FREECAD ASSEMBLY — COMPONENT RECIPES ("feeder_assembly")

This assembly document has 52 components, labeled P0..P51 below (a component is one placed body or linked part). 40 of them carry a construction recipe — the FreeCAD feature program that regenerates the part from scratch, quoted from this document or its linked companion documents; the rest are supplied as boundary geometry only. No exploded tour is included for this assembly.
NOTE — this tour is split across 3 documents so each fits a 32k-token context. This is document 1: the component sections continue in the remaining 2 documents, each repeating the header above.
COMPONENT P0 — recipe-attached ("Slide-left-Body", modeled in this document).
Construction recipe (the document's own serialized feature program — sketch geometry with constraints, then the solid features built on it; lengths are millimeters unless a unit is written):

FEATURE [Sketcher::SketchObject] Sketch
  FullyConstrained = true
  MapMode = 5
  Placement = pos=(0,0,0) rot=(0.57735,0.57735,0.57735;2.0944rad)
  Support = -> [YZ_Plane]
  sketch-geometry (4):
    g0: LineSegment StartX=0 StartY=0 StartZ=0 EndX=20 EndY=0 EndZ=0
    g1: LineSegment StartX=20 StartY=0 StartZ=0 EndX=20 EndY=30 EndZ=0
    g2: LineSegment StartX=20 StartY=30 StartZ=0 EndX=0 EndY=30 EndZ=0
    g3: LineSegment StartX=0 StartY=30 StartZ=0 EndX=0 EndY=0 EndZ=0
  constraints (11):
    c: Coincident(g0,g1)
    c: Coincident(g1,g2)
    c: Coincident(g2,g3)
    c: Coincident(g3,g0)
    c: Horizontal(g0)
    c: Horizontal(g2)
    c: Vertical(g1)
    c: Vertical(g3)
    c: Coincident(g0,g-1)
    c: DistanceY(g3,g3) = 30
    c: DistanceX(g0,g0) = 20
FEATURE [PartDesign::Pad] Pad  label="Pad-body001"
  Direction = (1,-2e-16,3e-16)
  Length = 200
  Length2 = 10
  Placement = pos=(0,0,0) rot=(0.57735,0.57735,0.57735;2.0944rad)
  Profile = -> Sketch
  ReferenceAxis = -> Sketch [N_Axis]
  Type = 0
FEATURE [Sketcher::SketchObject] Sketch008
  FullyConstrained = true
  MapMode = 5
  Placement = pos=(8.8e-15,20,-4.4e-15) rot=(0.57735,0.57735,0.57735;4.18879rad)
  Support = -> [Pad]
  sketch-geometry (5):
    g0: Circle CenterX=15 CenterY=10 CenterZ=0 NormalX=0 NormalY=0 NormalZ=1 AngleXU=0 Radius=5
    g1: ArcOfCircle CenterX=15 CenterY=190 CenterZ=0 NormalX=0 NormalY=0 NormalZ=1 AngleXU=0 Radius=5 StartAngle=1.7e-15 EndAngle=3.14159
    g2: ArcOfCircle CenterX=15 CenterY=35 CenterZ=0 NormalX=0 NormalY=0 NormalZ=1 AngleXU=0 Radius=5 StartAngle=3.14159 EndAngle=6.28319
    g3: LineSegment StartX=10 StartY=190 StartZ=0 EndX=10 EndY=35 EndZ=0
    g4: LineSegment StartX=20 StartY=35 StartZ=0 EndX=20 EndY=190 EndZ=0
  constraints (13):
    c: Diameter(g0) = 10
    c: DistanceX(g-1,g0) = 15
    c: DistanceY(g-1,g0) = 10
    c: Tangent(g1,g3) = -1.5708
    c: Tangent(g3,g2) = -1.5708
    c: Tangent(g2,g4) = -1.5708
    c: Tangent(g4,g1) = -1.5708
    c: Equal(g1,g2)
    c: Vertical(g3)
    c: Radius(g2) = 5
    c: Vertical(g2,g0)
    c: DistanceY(g0,g2) = 25
    c: DistanceY(g0,g1) = 180
FEATURE [PartDesign::Pocket] Pocket  label="Pocket-slider_guide"
  BaseFeature = -> Pad
  Direction = (-3e-16,-1,1e-16)
  Length = 5
  Length2 = 5
  Placement = pos=(0,0,0) rot=(0.57735,0.57735,0.57735;2.0944rad)
  Profile = -> Sketch008
  ReferenceAxis = -> Sketch008 [N_Axis]
  Type = 1
FEATURE [Sketcher::SketchObject] Sketch009
  FullyConstrained = true
  MapMode = 5
  Placement = pos=(-8.4e-15,1.32e-14,30) rot=(0,0,-1;1.5708rad)
  Support = -> [Pocket]
  sketch-geometry (2):
    g0: Circle CenterX=-10 CenterY=50 CenterZ=0 NormalX=0 NormalY=0 NormalZ=1 AngleXU=0 Radius=3.1
    g1: Circle CenterX=-10 CenterY=180 CenterZ=0 NormalX=0 NormalY=0 NormalZ=1 AngleXU=0 Radius=3.1
  constraints (6):
    c: DistanceX(g0,g-1) = 10
    c: Vertical(g1,g0)
    c: DistanceY(g-1,g0) = 50
    c: DistanceY(g0,g1) = 130
    c: Diameter(g0) = 6.2
    c: Equal(g1,g0)
FEATURE [PartDesign::Pocket] Pocket001  label="Pocket-mount_holes"
  BaseFeature = -> Pocket
  Direction = (3e-16,-5e-16,-1)
  Length = 26.5
  Length2 = 5
  Placement = pos=(0,0,0) rot=(0.57735,0.57735,0.57735;2.0944rad)
  Profile = -> Sketch009
  ReferenceAxis = -> Sketch009 [N_Axis]
  Type = 0
FEATURE [Sketcher::SketchObject] Sketch013  label="Sketch-slider_guide_line"
  FullyConstrained = false
  MapMode = 5
  Placement = pos=(0,1e-16,0) rot=(-0.57735,-0.57735,0.57735;4.18879rad)
  Support = -> [Pocket001]
  sketch-geometry (1):
    g0: LineSegment StartX=-14.7121 StartY=24.4994 StartZ=0 EndX=-14.7121 EndY=187.74 EndZ=0
  constraints (1):
    c: Vertical(g0)
FEATURE [Sketcher::SketchObject] Sketch023
  ExternalGeometry = -> [Pocket001]
  FullyConstrained = true
  MapMode = 5
  Placement = pos=(0,0,0) rot=(0.57735,0.57735,-0.57735;4.18879rad)
  Support = -> [Pocket001]
  sketch-geometry (8):
    g0: LineSegment StartX=-10 StartY=2.5 StartZ=0 EndX=-10 EndY=-52.5 EndZ=0
    g1: LineSegment StartX=0 StartY=0 StartZ=0 EndX=0 EndY=-30 EndZ=0
    g2: LineSegment StartX=0 StartY=-30 StartZ=0 EndX=20 EndY=-30 EndZ=0
    g3: GeomPoint X=0 Y=-15 Z=0
    g4: LineSegment StartX=4.24533 StartY=-52.5 StartZ=0 EndX=20 EndY=-30 EndZ=0
    g5: LineSegment StartX=-10 StartY=-52.5 StartZ=0 EndX=4.24533 EndY=-52.5 EndZ=0
    g6: LineSegment StartX=0 StartY=0 StartZ=0 EndX=-5 EndY=2.5 EndZ=0
    g7: LineSegment StartX=-5 StartY=2.5 StartZ=0 EndX=-10 EndY=2.5 EndZ=0
  constraints (20):
    c: Coincident(g6,g-4)
    c: Vertical(g0)
    c: Coincident(g5,g0)
    c: Coincident(g1,g6)
    c: Coincident(g0,g7)
    c: Coincident(g1,g2)
    c: Coincident(g1,g-4)
    c: DistanceX(g7,g6) = 10
    c: DistanceY(g0,g0) = 55
    c: PointOnObject(g3,g1)
    c: DistanceY(g3,g6) = 15
    c: DistanceY(g3,g7) = 17.5
    c: Horizontal(g5)
    c: Coincident(g5,g4)
    c: Coincident(g2,g4)
    c: Coincident(g2,g-3)
    c: Angle(g2,g4) = 0.959931
    c: Coincident(g6,g7)
    c: Horizontal(g7)
    c: DistanceX(g0,g6) = 5
FEATURE [PartDesign::Pad] Pad011
  BaseFeature = -> Pocket001
  Direction = (-1,2e-16,-2e-16)
  Length = 20
  Length2 = 10
  Placement = pos=(0,0,0) rot=(0.57735,0.57735,0.57735;2.0944rad)
  Profile = -> Sketch023
  ReferenceAxis = -> Sketch023 [N_Axis]
  Reversed = true
  Type = 0
FEATURE [Sketcher::SketchObject] Sketch025
  ExternalGeometry = -> [Pad011]
  FullyConstrained = true
  MapMode = 5
  Placement = pos=(-2.2e-15,-10,6e-16) rot=(-0.57735,-0.57735,0.57735;4.18879rad)
  Support = -> [Pad011]
  sketch-geometry (15):
    g0: Circle CenterX=-49.575 CenterY=14.9 CenterZ=0 NormalX=0 NormalY=0 NormalZ=1 AngleXU=0 Radius=1.125
    g1: Circle CenterX=-49.575 CenterY=5.1 CenterZ=0 NormalX=0 NormalY=0 NormalZ=1 AngleXU=0 Radius=1.125
    g2: Circle CenterX=-1.125 CenterY=14.9 CenterZ=0 NormalX=0 NormalY=0 NormalZ=1 AngleXU=0 Radius=1.125
    g3: Circle CenterX=-1.125 CenterY=5.1 CenterZ=0 NormalX=0 NormalY=0 NormalZ=1 AngleXU=0 Radius=1.125
    g4: LineSegment StartX=-46.35 StartY=0 StartZ=0 EndX=-4.35 EndY=0 EndZ=0
    g5: LineSegment StartX=-4.35 StartY=0 StartZ=0 EndX=-4.35 EndY=20 EndZ=0
    g6: LineSegment StartX=-4.35 StartY=20 StartZ=0 EndX=-46.35 EndY=20 EndZ=0
    g7: LineSegment StartX=-46.35 StartY=20 StartZ=0 EndX=-46.35 EndY=0 EndZ=0
    g8: LineSegment StartX=-49.575 StartY=14.9 StartZ=0 EndX=-49.575 EndY=5.1 EndZ=0
    g9: LineSegment StartX=-49.575 StartY=5.1 StartZ=0 EndX=-1.125 EndY=5.1 EndZ=0
    g10: LineSegment StartX=-1.125 StartY=14.9 StartZ=0 EndX=-49.575 EndY=14.9 EndZ=0
    g11: LineSegment StartX=-46.35 StartY=20 StartZ=0 EndX=-49.575 EndY=14.9 EndZ=0
    g12: LineSegment StartX=-4.35 StartY=20 StartZ=0 EndX=-1.125 EndY=14.9 EndZ=0
    g13: LineSegment StartX=-1.125 StartY=5.1 StartZ=0 EndX=-1.125 EndY=10 EndZ=0
    g14: LineSegment StartX=-1.125 StartY=10 StartZ=0 EndX=-1.125 EndY=14.9 EndZ=0
  constraints (39):
    c: Tangent(g3,g-2)
    c: Coincident(g4,g5)
    c: Coincident(g5,g6)
    c: Coincident(g6,g7)
    c: Coincident(g7,g4)
    c: Horizontal(g4)
    c: Horizontal(g6)
    c: Vertical(g5)
    c: Vertical(g7)
    c: Horizontal(g-4,g5)
    c: DistanceX(g6,g6) = 42
    c: Diameter(g2) = 2.25
    c: Equal(g0,g1)
    c: Equal(g1,g3)
    c: Equal(g3,g2)
    c: Coincident(g8,g0)
    c: Coincident(g8,g1)
    c: Vertical(g8)
    c: Coincident(g9,g1)
    c: Coincident(g9,g3)
    c: Horizontal(g9)
    c: Coincident(g13,g3)
    c: Coincident(g14,g2)
    c: Coincident(g10,g2)
    c: Coincident(g10,g0)
    c: Horizontal(g10)
    c: Coincident(g11,g6)
    c: Coincident(g11,g0)
    c: Coincident(g12,g5)
    c: Coincident(g12,g2)
    c: Equal(g12,g11)
    c: DistanceX(g9,g9) = 48.45
    c: DistanceY(g8,g8) = 9.8
    c: Coincident(g13,g14)
    c: Vertical(g13)
    c: Vertical(g14)
    c: Equal(g14,g13)
    c: DistanceY(g-4,g13) = 10
    c: PointOnObject(g4,g-5)
FEATURE [PartDesign::Pocket] Pocket008
  BaseFeature = -> Pad011
  Direction = (1e-16,1,1e-16)
  Length = 10
  Length2 = 5
  Placement = pos=(0,0,0) rot=(0.57735,0.57735,0.57735;2.0944rad)
  Profile = -> Sketch025
  ReferenceAxis = -> Sketch025 [N_Axis]
  Type = 0
FEATURE [Sketcher::SketchObject] Sketch026
  ExternalGeometry = -> [Pocket008]
  FullyConstrained = true
  MapMode = 5
  Placement = pos=(-1.47e-14,0,52.5) rot=(0,0,-1;1.5708rad)
  Support = -> [Pocket008]
  sketch-geometry (4):
    g0: LineSegment StartX=-20 StartY=17.5 StartZ=0 EndX=5 EndY=17.5 EndZ=0
    g1: LineSegment StartX=5 StartY=17.5 StartZ=0 EndX=5 EndY=2.5 EndZ=0
    g2: LineSegment StartX=5 StartY=2.5 StartZ=0 EndX=-20 EndY=2.5 EndZ=0
    g3: LineSegment StartX=-20 StartY=2.5 StartZ=0 EndX=-20 EndY=17.5 EndZ=0
  constraints (12):
    c: Coincident(g0,g1)
    c: Coincident(g1,g2)
    c: Coincident(g2,g3)
    c: Coincident(g3,g0)
    c: Horizontal(g0)
    c: Horizontal(g2)
    c: Vertical(g1)
    c: Vertical(g3)
    c: DistanceX(g2,g2) = 25
    c: DistanceX(g1,g-3) = 5
    c: DistanceY(g-3,g1) = 2.5
    c: DistanceY(g0,g-4) = 2.5
FEATURE [PartDesign::Pocket] Pocket009
  BaseFeature = -> Pocket008
  Direction = (3e-16,-1e-16,-1)
  Length = 6
  Length2 = 5
  Placement = pos=(0,0,0) rot=(0.57735,0.57735,0.57735;2.0944rad)
  Profile = -> Sketch026
  ReferenceAxis = -> Sketch026 [N_Axis]
  Type = 0
FEATURE [Sketcher::SketchObject] Sketch027
  ExternalGeometry = -> [Pocket009]
  FullyConstrained = true
  MapMode = 5
  Placement = pos=(7e-16,0,-2.5) rot=(0.707107,0.707107,0;3.14159rad)
  Support = -> [Pocket009]
  sketch-geometry (4):
    g0: LineSegment StartX=-5 StartY=17.5 StartZ=0 EndX=5 EndY=17.5 EndZ=0
    g1: LineSegment StartX=5 StartY=17.5 StartZ=0 EndX=5 EndY=2.5 EndZ=0
    g2: LineSegment StartX=5 StartY=2.5 StartZ=0 EndX=-5 EndY=2.5 EndZ=0
    g3: LineSegment StartX=-5 StartY=2.5 StartZ=0 EndX=-5 EndY=17.5 EndZ=0
  constraints (12):
    c: Coincident(g0,g1)
    c: Coincident(g1,g2)
    c: Coincident(g2,g3)
    c: Coincident(g3,g0)
    c: Horizontal(g0)
    c: Horizontal(g2)
    c: Vertical(g1)
    c: Vertical(g3)
    c: DistanceX(g-3,g2) = 5
    c: DistanceY(g-3,g2) = 2.5
    c: DistanceY(g0,g-3) = 2.5
    c: DistanceX(g0,g0) = 10
FEATURE [PartDesign::Pocket] Pocket010
  BaseFeature = -> Pocket009
  Direction = (-3e-16,1e-16,1)
  Length = 6
  Length2 = 5
  Placement = pos=(0,0,0) rot=(0.57735,0.57735,0.57735;2.0944rad)
  Profile = -> Sketch027
  ReferenceAxis = -> Sketch027 [N_Axis]
  Type = 0
FEATURE [Sketcher::SketchObject] Sketch030
  FullyConstrained = true
  MapMode = 5
  Placement = pos=(-8.4e-15,1.32e-14,30) rot=(0,0,-1;1.5708rad)
  Support = -> [Pocket010]
  sketch-geometry (8):
    g0: ArcOfCircle CenterX=-10 CenterY=40 CenterZ=0 NormalX=0 NormalY=0 NormalZ=1 AngleXU=0 Radius=6 StartAngle=3.14159 EndAngle=6.28319
    g1: ArcOfCircle CenterX=-10 CenterY=80 CenterZ=0 NormalX=0 NormalY=0 NormalZ=1 AngleXU=0 Radius=6 StartAngle=-1.8e-15 EndAngle=3.14159
    g2: LineSegment StartX=-4 StartY=40 StartZ=0 EndX=-4 EndY=80 EndZ=0
    g3: LineSegment StartX=-16 StartY=80 StartZ=0 EndX=-16 EndY=40 EndZ=0
    g4: ArcOfCircle CenterX=-10 CenterY=180 CenterZ=0 NormalX=0 NormalY=0 NormalZ=1 AngleXU=0 Radius=6 StartAngle=2.9e-15 EndAngle=3.14159
    g5: ArcOfCircle CenterX=-10 CenterY=140 CenterZ=0 NormalX=0 NormalY=0 NormalZ=1 AngleXU=0 Radius=6 StartAngle=3.14159 EndAngle=6.28319
    g6: LineSegment StartX=-16 StartY=180 StartZ=0 EndX=-16 EndY=140 EndZ=0
    g7: LineSegment StartX=-4 StartY=140 StartZ=0 EndX=-4 EndY=180 EndZ=0
  constraints (20):
    c: Tangent(g0,g2) = -1.5708
    c: Tangent(g2,g1) = -1.5708
    c: Tangent(g1,g3) = -1.5708
    c: Tangent(g3,g0) = -1.5708
    c: Equal(g0,g1)
    c: Vertical(g2)
    c: Diameter(g1) = 12
    c: DistanceY(g2,g2) = 40
    c: DistanceX(g-1,g0) = -10
    c: DistanceY(g-1,g0) = 40
    c: Tangent(g4,g6) = -1.5708
    c: Tangent(g6,g5) = -1.5708
    c: Tangent(g5,g7) = -1.5708
    c: Tangent(g7,g4) = -1.5708
    c: Equal(g4,g5)
    c: Vertical(g6)
    c: DistanceY(g1,g5) = 60
    c: DistanceY(g7,g7) = 40
    c: Diameter(g5) = 12
    c: Vertical(g5,g1)
FEATURE [PartDesign::Pocket] Pocket012
  BaseFeature = -> Pocket010
  Direction = (3e-16,-8e-16,-1)
  Length = 26.5
  Length2 = 5
  Placement = pos=(0,0,0) rot=(0.57735,0.57735,0.57735;2.0944rad)
  Profile = -> Sketch030
  ReferenceAxis = -> Sketch030 [N_Axis]
  Type = 0
FEATURE [Sketcher::SketchObject] Sketch031
  FullyConstrained = true
  MapMode = 5
  Placement = pos=(-8.4e-15,1.32e-14,30) rot=(0,0,-1;1.5708rad)
  Support = -> [Pocket012]
  sketch-geometry (4):
    g0: Circle CenterX=-10 CenterY=45 CenterZ=0 NormalX=0 NormalY=0 NormalZ=1 AngleXU=0 Radius=3.1
    g1: Circle CenterX=-10 CenterY=75 CenterZ=0 NormalX=0 NormalY=0 NormalZ=1 AngleXU=0 Radius=3.1
    g2: Circle CenterX=-10 CenterY=145 CenterZ=0 NormalX=0 NormalY=0 NormalZ=1 AngleXU=0 Radius=3.1
    g3: Circle CenterX=-10 CenterY=175 CenterZ=0 NormalX=0 NormalY=0 NormalZ=1 AngleXU=0 Radius=3.1
  constraints (12):
    c: Equal(g0,g1)
    c: Equal(g1,g2)
    c: Equal(g2,g3)
    c: Vertical(g3,g2)
    c: Vertical(g2,g1)
    c: Vertical(g1,g0)
    c: DistanceX(g0,g-1) = 10
    c: DistanceY(g-1,g0) = 45
    c: DistanceY(g0,g1) = 30
    c: DistanceY(g1,g2) = 70
    c: DistanceY(g2,g3) = 30
    c: Diameter(g2) = 6.2
FEATURE [PartDesign::Pocket] Pocket013
  BaseFeature = -> Pocket012
  Direction = (3e-16,-8e-16,-1)
  Length = 5
  Length2 = 5
  Placement = pos=(0,0,0) rot=(0.57735,0.57735,0.57735;2.0944rad)
  Profile = -> Sketch031
  ReferenceAxis = -> Sketch031 [N_Axis]
  Type = 1
FEATURE [Sketcher::SketchObject] Sketch032
  ExternalGeometry = -> [Pocket013]
  FullyConstrained = true
  MapMode = 5
  Placement = pos=(-1.47e-14,0,52.5) rot=(0,0,-1;1.5708rad)
  Support = -> [Pocket013]
  sketch-geometry (6):
    g0: LineSegment StartX=10 StartY=11 StartZ=0 EndX=8 EndY=11 EndZ=0
    g1: LineSegment StartX=8 StartY=11 StartZ=0 EndX=8 EndY=9 EndZ=0
    g2: LineSegment StartX=8 StartY=9 StartZ=0 EndX=10 EndY=9 EndZ=0
    g3: LineSegment StartX=10 StartY=9 StartZ=0 EndX=10 EndY=11 EndZ=0
    g4: LineSegment StartX=10 StartY=20 StartZ=0 EndX=8 EndY=11 EndZ=0
    g5: LineSegment StartX=8 StartY=9 StartZ=0 EndX=10 EndY=-3.6e-15 EndZ=0
  constraints (16):
    c: Coincident(g0,g1)
    c: Coincident(g1,g2)
    c: Coincident(g2,g3)
    c: Coincident(g3,g0)
    c: Horizontal(g0)
    c: Horizontal(g2)
    c: Vertical(g1)
    c: Vertical(g3)
    c: PointOnObject(g0,g-3)
    c: DistanceX(g2,g2) = 2
    c: DistanceY(g1,g1) = 2
    c: Coincident(g4,g-3)
    c: Coincident(g4,g0)
    c: Coincident(g5,g1)
    c: Coincident(g5,g-3)
    c: Equal(g4,g5)
FEATURE [PartDesign::Pocket] Pocket014
  BaseFeature = -> Pocket013
  Direction = (3e-16,-3e-16,-1)
  Length = 5
  Length2 = 5
  Placement = pos=(0,0,0) rot=(0.57735,0.57735,0.57735;2.0944rad)
  Profile = -> Sketch032
  ReferenceAxis = -> Sketch032 [N_Axis]
  Type = 1
FEATURE [PartDesign::Body] Body  label="Slide-left-Body"
  Group = -> [Sketch,Pad,Sketch008,Pocket,Sketch009,Pocket001,Sketch013,Sketch023,Pad011,Sketch025,Pocket008,Sketch026,Pocket009,Sketch027,Pocket010,Sketch030,Pocket012,Sketch031,Pocket013,Sketch032,Pocket014]
  Origin = -> Origin
  Placement = pos=(-375,53,160) rot=(0,0,-1;1.5708rad)
  Tip = -> Pocket014
COMPONENT P1 — recipe-attached ("Door-back-Body", modeled in this document).
Construction recipe (the document's own serialized feature program — sketch geometry with constraints, then the solid features built on it; lengths are millimeters unless a unit is written):

FEATURE [Sketcher::SketchObject] Sketch001
  FullyConstrained = true
  MapMode = 5
  Support = -> [XY_Plane001]
  sketch-geometry (4):
    g0: LineSegment StartX=0 StartY=50 StartZ=0 EndX=166 EndY=50 EndZ=0
    g1: LineSegment StartX=166 StartY=50 StartZ=0 EndX=166 EndY=140 EndZ=0
    g2: LineSegment StartX=166 StartY=140 StartZ=0 EndX=0 EndY=140 EndZ=0
    g3: LineSegment StartX=0 StartY=140 StartZ=0 EndX=0 EndY=50 EndZ=0
  constraints (12):
    c: Coincident(g0,g1)
    c: Coincident(g1,g2)
    c: Coincident(g2,g3)
    c: Coincident(g3,g0)
    c: Horizontal(g0)
    c: Horizontal(g2)
    c: Vertical(g1)
    c: Vertical(g3)
    c: PointOnObject(g0,g-2)
    c: DistanceY(g1,g1) = 90
    c: DistanceX(g0,g0) = 166
    c: DistanceY(g-1,g2) = 140
FEATURE [PartDesign::Pad] Pad001  label="Pad-base_rect"
  Direction = (0,0,1)
  Length = 5
  Length2 = 10
  Profile = -> Sketch001
  ReferenceAxis = -> Sketch001 [N_Axis]
  Type = 0
FEATURE [Sketcher::SketchObject] Sketch002
  ExternalGeometry = -> [Pad001]
  FullyConstrained = true
  MapMode = 5
  Placement = pos=(0,0,0) rot=(0.57735,-0.57735,-0.57735;2.0944rad)
  Support = -> [Pad001]
  sketch-geometry (1):
    g0: Circle CenterX=-140 CenterY=2.5 CenterZ=0 NormalX=0 NormalY=0 NormalZ=1 AngleXU=0 Radius=4.5
  constraints (3):
    c: DistanceY(g-3,g0) = 2.5
    c: Diameter(g0) = 9
    c: PointOnObject(g0,g-3)
FEATURE [PartDesign::Pad] Pad002  label="Pad-base_9mm_shaft"
  BaseFeature = -> Pad001
  Direction = (-1,0,0)
  Length = 21
  Length2 = 177
  Profile = -> Sketch002
  ReferenceAxis = -> Sketch002 [N_Axis]
  Type = 4
FEATURE [Sketcher::SketchObject] Sketch014
  ExternalGeometry = -> [Pad002]
  FullyConstrained = true
  MapMode = 5
  Placement = pos=(0,0,0) rot=(1,0,0;3.14159rad)
  Support = -> [Pad002]
  sketch-geometry (18):
    g0: LineSegment StartX=10 StartY=-45.5 StartZ=0 EndX=15 EndY=-45.5 EndZ=0
    g1: LineSegment StartX=15 StartY=-45.5 StartZ=0 EndX=15 EndY=-60.5 EndZ=0
    g2: LineSegment StartX=15 StartY=-60.5 StartZ=0 EndX=10 EndY=-60.5 EndZ=0
    g3: LineSegment StartX=10 StartY=-60.5 StartZ=0 EndX=10 EndY=-45.5 EndZ=0
    g4: LineSegment StartX=25.5 StartY=-45.5 StartZ=0 EndX=30.5 EndY=-45.5 EndZ=0
    g5: LineSegment StartX=30.5 StartY=-45.5 StartZ=0 EndX=30.5 EndY=-60.5 EndZ=0
    g6: LineSegment StartX=30.5 StartY=-60.5 StartZ=0 EndX=25.5 EndY=-60.5 EndZ=0
    g7: LineSegment StartX=25.5 StartY=-60.5 StartZ=0 EndX=25.5 EndY=-45.5 EndZ=0
    g8: LineSegment StartX=135.5 StartY=-45.5 StartZ=0 EndX=140.5 EndY=-45.5 EndZ=0
    g9: LineSegment StartX=140.5 StartY=-45.5 StartZ=0 EndX=140.5 EndY=-60.5 EndZ=0
    g10: LineSegment StartX=140.5 StartY=-60.5 StartZ=0 EndX=135.5 EndY=-60.5 EndZ=0
    g11: LineSegment StartX=135.5 StartY=-60.5 StartZ=0 EndX=135.5 EndY=-45.5 EndZ=0
    g12: LineSegment StartX=151 StartY=-45.5 StartZ=0 EndX=156 EndY=-45.5 EndZ=0
    g13: LineSegment StartX=156 StartY=-45.5 StartZ=0 EndX=156 EndY=-60.5 EndZ=0
    g14: LineSegment StartX=156 StartY=-60.5 StartZ=0 EndX=151 EndY=-60.5 EndZ=0
    g15: LineSegment StartX=151 StartY=-60.5 StartZ=0 EndX=151 EndY=-45.5 EndZ=0
    g16: LineSegment StartX=15 StartY=-60.5 StartZ=0 EndX=25.5 EndY=-60.5 EndZ=0
    g17: LineSegment StartX=140.5 StartY=-60.5 StartZ=0 EndX=151 EndY=-60.5 EndZ=0
  constraints (52):
    c: Coincident(g0,g1)
    c: Coincident(g1,g2)
    c: Coincident(g2,g3)
    c: Coincident(g3,g0)
    c: Horizontal(g0)
    c: Horizontal(g2)
    c: Vertical(g1)
    c: Vertical(g3)
    c: Coincident(g4,g5)
    c: Coincident(g5,g6)
    c: Coincident(g6,g7)
    c: Coincident(g7,g4)
    c: Horizontal(g4)
    c: Horizontal(g6)
    c: Vertical(g5)
    c: Vertical(g7)
    c: Coincident(g8,g9)
    c: Coincident(g9,g10)
    c: Coincident(g10,g11)
    c: Coincident(g11,g8)
    c: Horizontal(g8)
    c: Horizontal(g10)
    c: Vertical(g9)
    c: Vertical(g11)
    c: Coincident(g12,g13)
    c: Coincident(g13,g14)
    c: Coincident(g14,g15)
    c: Coincident(g15,g12)
    c: Horizontal(g12)
    c: Horizontal(g14)
    c: Vertical(g13)
    c: Vertical(g15)
    c: Horizontal(g6,g10)
    c: Horizontal(g0,g4)
    c: Horizontal(g4,g8)
    c: Horizontal(g8,g12)
    c: Equal(g2,g6)
    c: Equal(g6,g10)
    c: Equal(g10,g14)
    c: DistanceX(g-1,g2) = 10
    c: DistanceX(g2,g2) = 5
    c: DistanceX(g1,g6) = 10.5
    c: DistanceY(g3,g3) = 15
    c: Coincident(g16,g1)
    c: Coincident(g16,g6)
    c: Horizontal(g16)
    c: Coincident(g17,g9)
    c: Coincident(g17,g14)
    c: Horizontal(g17)
    c: Equal(g16,g17)
    c: DistanceX(g12,g-3) = 10
    c: DistanceY(g-3,g0) = 4.5
FEATURE [PartDesign::Pad] Pad008  label="Pad-left_right_hinges"
  BaseFeature = -> Pad002
  Direction = (0,0,-1)
  Length = 7
  Length2 = 10
  Profile = -> Sketch014
  ReferenceAxis = -> Sketch014 [N_Axis]
  Type = 0
FEATURE [Sketcher::SketchObject] Sketch015
  ExternalGeometry = -> [Pad008]
  FullyConstrained = true
  MapMode = 5
  Placement = pos=(10,0,0) rot=(0.57735,-0.57735,-0.57735;2.0944rad)
  Support = -> [Pad008]
  sketch-geometry (4):
    g0: Circle CenterX=-49 CenterY=-3.5 CenterZ=0 NormalX=0 NormalY=0 NormalZ=1 AngleXU=0 Radius=1.75
    g1: LineSegment StartX=-60.5 StartY=0 StartZ=0 EndX=-53.5 EndY=-7 EndZ=0
    g2: LineSegment StartX=-53.5 StartY=-7 StartZ=0 EndX=-60.5 EndY=-7 EndZ=0
    g3: LineSegment StartX=-60.5 StartY=-7 StartZ=0 EndX=-60.5 EndY=0 EndZ=0
  constraints (12):
    c: Diameter(g0) = 3.5
    c: DistanceX(g-3,g0) = 1
    c: DistanceY(g0,g-3) = 3.5
    c: PointOnObject(g1,g-1)
    c: Coincident(g2,g1)
    c: Horizontal(g2)
    c: Coincident(g3,g2)
    c: Coincident(g3,g1)
    c: Vertical(g3)
    c: DistanceY(g3,g3) = 7
    c: Angle(g3,g1) = 0.785398
    c: DistanceX(g1,g-3) = 10.5
FEATURE [PartDesign::Pocket] Pocket004  label="Pocket-left_right_hinge2"
  BaseFeature = -> Pad008
  Direction = (1,0,0)
  Length = 5
  Length2 = 5
  Profile = -> Sketch015
  ReferenceAxis = -> Sketch015 [N_Axis]
  Type = 1
FEATURE [Sketcher::SketchObject] Sketch028
  ExternalGeometry = -> [Pocket004]
  FullyConstrained = true
  MapMode = 5
  Placement = pos=(-21,0,0) rot=(0.57735,-0.57735,-0.57735;2.0944rad)
  Support = -> [Pocket004]
  sketch-geometry (5):
    g0: LineSegment StartX=-140 StartY=2.5 StartZ=0 EndX=-140 EndY=5.6 EndZ=0
    g1: LineSegment StartX=-140 StartY=5.6 StartZ=0 EndX=-139.662 EndY=5.17871 EndZ=0
    g2: LineSegment StartX=-139.662 StartY=5.17871 StartZ=0 EndX=-139.229 EndY=5.50261 EndZ=0
    g3: LineSegment StartX=-139.229 StartY=5.50261 StartZ=0 EndX=-140 EndY=2.5 EndZ=0
    g4: LineSegment StartX=-140 StartY=2.5 StartZ=0 EndX=-139.662 EndY=5.17871 EndZ=0
  constraints (13):
    c: Coincident(g0,g-3)
    c: Coincident(g1,g0)
    c: Coincident(g2,g1)
    c: Coincident(g3,g2)
    c: Coincident(g3,g0)
    c: Distance(g0) = 3.1
    c: Distance(g3) = 3.1
    c: Coincident(g4,g0)
    c: Coincident(g4,g1)
    c: Angle(g4,g0) = 0.125664
    c: Angle(g3,g0) = 0.251327
    c: Distance(g4) = 2.7
    c: Vertical(g0)
FEATURE [PartDesign::Pocket] Pocket011  label="Pocket-spline-single"
  BaseFeature = -> Pocket004
  Direction = (1,0,0)
  Length = 4
  Length2 = 5
  Profile = -> Sketch028
  ReferenceAxis = -> Sketch028 [N_Axis]
  Type = 0
FEATURE [PartDesign::PolarPattern] PolarPattern
  Angle = 360
  Axis = -> Pocket011 [Edge104]
  BaseFeature = -> Pocket011
  Occurrences = 25
  Originals = -> [Pocket011]
FEATURE [PartDesign::Fillet] Fillet
  Base = -> PolarPattern [Edge34,Edge74,Edge81,Edge39,Edge44,Edge49,Edge95,Edge88]
  BaseFeature = -> PolarPattern
  Radius = 3.4
  SupportTransform = false
  UseAllEdges = false
FEATURE [PartDesign::Chamfer] Chamfer
  Angle = 45
  Base = -> Fillet [Edge16,Edge17,Edge19,Edge23,Edge21]
  BaseFeature = -> Fillet
  ChamferType = 0
  FlipDirection = false
  Size = 3
  Size2 = 1
  SupportTransform = false
  UseAllEdges = false
FEATURE [Sketcher::SketchObject] Sketch067
  ExternalGeometry = -> [Chamfer]
  FullyConstrained = false
  MapMode = 5
  Placement = pos=(-21,0,0) rot=(0.57735,-0.57735,-0.57735;2.0944rad)
  Support = -> [Chamfer]
  sketch-geometry (1):
    g0: Circle CenterX=-140 CenterY=2.5 CenterZ=0 NormalX=0 NormalY=0 NormalZ=1 AngleXU=0 Radius=6
  constraints (1):
    c: Diameter(g0) = 12
FEATURE [PartDesign::Pad] Pad025  label="Pad-thicker_shaft"
  BaseFeature = -> Chamfer
  Direction = (-1,0,0)
  Length = 1
  Length2 = 198
  Profile = -> Sketch067
  ReferenceAxis = -> Sketch067 [N_Axis]
  Type = 4
FEATURE [Sketcher::SketchObject] Sketch068
  ExternalGeometry = -> [Pocket004]
  FullyConstrained = true
  MapMode = 5
  Placement = pos=(-21,0,0) rot=(0.57735,-0.57735,-0.57735;2.0944rad)
  Support = -> [Pocket004]
  sketch-geometry (5):
    g0: LineSegment StartX=-140 StartY=2.5 StartZ=0 EndX=-140 EndY=5.6 EndZ=0
    g1: LineSegment StartX=-140 StartY=5.6 StartZ=0 EndX=-139.662 EndY=5.17871 EndZ=0
    g2: LineSegment StartX=-139.662 StartY=5.17871 StartZ=0 EndX=-139.229 EndY=5.50261 EndZ=0
    g3: LineSegment StartX=-139.229 StartY=5.50261 StartZ=0 EndX=-140 EndY=2.5 EndZ=0
    g4: LineSegment StartX=-140 StartY=2.5 StartZ=0 EndX=-139.662 EndY=5.17871 EndZ=0
  constraints (13):
    c: Coincident(g0,g-3)
    c: Coincident(g1,g0)
    c: Coincident(g2,g1)
    c: Coincident(g3,g2)
    c: Coincident(g3,g0)
    c: Distance(g0) = 3.1
    c: Distance(g3) = 3.1
    c: Coincident(g4,g0)
    c: Coincident(g4,g1)
    c: Angle(g4,g0) = 0.125664
    c: Angle(g3,g0) = 0.251327
    c: Distance(g4) = 2.7
    c: Vertical(g0)
FEATURE [PartDesign::Pocket] Pocket034  label="Pocket-spline2"
  BaseFeature = -> Pad025
  Direction = (1,0,0)
  Length = 4
  Length2 = 5
  Profile = -> Sketch068
  ReferenceAxis = -> Sketch068 [N_Axis]
  Type = 4
FEATURE [PartDesign::PolarPattern] PolarPattern001
  Angle = 360
  Axis = -> Pocket034 [Edge157]
  BaseFeature = -> Pocket034
  Occurrences = 25
  Originals = -> [Pocket034]
FEATURE [Sketcher::SketchObject] Sketch075
  ExternalGeometry = -> [PolarPattern001]
  FullyConstrained = true
  MapMode = 5
  Placement = pos=(177,0,0) rot=(0.57735,0.57735,0.57735;2.0944rad)
  Support = -> [PolarPattern001]
  sketch-geometry (2):
    g0: Circle CenterX=140 CenterY=2.5 CenterZ=0 NormalX=0 NormalY=0 NormalZ=1 AngleXU=0 Radius=3.95
    g1: Circle CenterX=140 CenterY=2.5 CenterZ=0 NormalX=0 NormalY=0 NormalZ=1 AngleXU=0 Radius=7.565
  constraints (4):
    c: Coincident(g0,g-3)
    c: Coincident(g1,g0)
    c: Diameter(g0) = 7.9
    c: Diameter(g1) = 15.13
FEATURE [PartDesign::Pocket] Pocket037  label="Pocket-neck_down_bearing"
  BaseFeature = -> PolarPattern001
  Direction = (-1,0,0)
  Length = 10
  Length2 = 5
  Profile = -> Sketch075
  ReferenceAxis = -> Sketch075 [N_Axis]
  Type = 0
FEATURE [Sketcher::SketchObject] Sketch076
  ExternalGeometry = -> [Pocket037]
  FullyConstrained = true
  MapMode = 5
  Placement = pos=(177,0,0) rot=(0.57735,0.57735,0.57735;2.0944rad)
  Support = -> [Pocket037]
  sketch-geometry (1):
    g0: Circle CenterX=140 CenterY=2.5 CenterZ=0 NormalX=0 NormalY=0 NormalZ=1 AngleXU=0 Radius=7.5
  constraints (2):
    c: Coincident(g0,g-3)
    c: Diameter(g0) = 15
FEATURE [PartDesign::Pocket] Pocket038  label="Pocket-shorten_down_bearing_shaft"
  BaseFeature = -> Pocket037
  Direction = (-1,0,0)
  Length = 2
  Length2 = 5
  Profile = -> Sketch076
  ReferenceAxis = -> Sketch076 [N_Axis]
  Type = 0
FEATURE [PartDesign::Fillet] Fillet010  label="Fillet-bearing_shaft_corner"
  Base = -> Pocket038 [Edge135]
  BaseFeature = -> Pocket038
  Radius = 0.2
  SupportTransform = false
  UseAllEdges = false
FEATURE [PartDesign::Fillet] Fillet011  label="Fillet-shaft_end"
  Base = -> Fillet010 [Edge2,Edge15]
  BaseFeature = -> Fillet010
  Radius = 0.5
  SupportTransform = false
  UseAllEdges = false
FEATURE [PartDesign::Fillet] Fillet012
  Base = -> Fillet011 [Edge12,Edge9]
  BaseFeature = -> Fillet011
  Radius = 5
  SupportTransform = false
  UseAllEdges = false
FEATURE [Sketcher::SketchObject] Sketch240
  ExternalGeometry = -> [Fillet012]
  FullyConstrained = true
  MapMode = 5
  Placement = pos=(-22,0,0) rot=(0.57735,-0.57735,-0.57735;2.0944rad)
  Support = -> [Fillet012]
  sketch-geometry (2):
    g0: Circle CenterX=-140 CenterY=2.5 CenterZ=0 NormalX=0 NormalY=0 NormalZ=1 AngleXU=0 Radius=7.5
    g1: Circle CenterX=-140 CenterY=2.5 CenterZ=0 NormalX=0 NormalY=0 NormalZ=1 AngleXU=0 Radius=6
  constraints (4):
    c: Coincident(g0,g-3)
    c: Diameter(g0) = 15
    c: Coincident(g1,g0)
    c: Equal(g-3,g1)
FEATURE [PartDesign::Pad] Pad121
  BaseFeature = -> Fillet012
  Direction = (-1,0,0)
  Length = 40
  Length2 = 10
  Profile = -> Sketch240
  ReferenceAxis = -> Sketch240 [N_Axis]
  Reversed = true
  Type = 0
FEATURE [PartDesign::Fillet] Fillet127
  Base = -> Pad121 [Edge27]
  BaseFeature = -> Pad121
  Radius = 1.4
  SupportTransform = false
  UseAllEdges = false
FEATURE [PartDesign::Fillet] Fillet128
  Base = -> Fillet127 [Edge1,Edge8]
  BaseFeature = -> Fillet127
  Radius = 1
  SupportTransform = false
  UseAllEdges = false
FEATURE [PartDesign::Body] Body001  label="Door-back-Body"
  Group = -> [Sketch001,Pad001,Sketch002,Pad002,Sketch014,Pad008,Sketch015,Pocket004,Sketch028,Pocket011,PolarPattern,Fillet,Chamfer,Sketch067,Pad025,Sketch068,Pocket034,PolarPattern001,Sketch075,Pocket037,Sketch076,Pocket038,Fillet010,Fillet011,Fillet012,Sketch240,Pad121,Fillet127,Fillet128]
  Origin = -> Origin001
  Placement = pos=(-363,-84,159) rot=(0,0,1;0rad)
  Tip = -> Fillet128
COMPONENT P2 — recipe-attached ("Body003", modeled in this document).
Construction recipe (the document's own serialized feature program — sketch geometry with constraints, then the solid features built on it; lengths are millimeters unless a unit is written):

FEATURE [Sketcher::SketchObject] Sketch004
  FullyConstrained = true
  MapMode = 5
  Support = -> [XY_Plane003]
  sketch-geometry (4):
    g0: LineSegment StartX=0 StartY=0 StartZ=0 EndX=166 EndY=0 EndZ=0
    g1: LineSegment StartX=166 StartY=0 StartZ=0 EndX=166 EndY=-90 EndZ=0
    g2: LineSegment StartX=166 StartY=-90 StartZ=0 EndX=0 EndY=-90 EndZ=0
    g3: LineSegment StartX=0 StartY=-90 StartZ=0 EndX=0 EndY=0 EndZ=0
  constraints (11):
    c: Coincident(g0,g1)
    c: Coincident(g1,g2)
    c: Coincident(g2,g3)
    c: Coincident(g3,g0)
    c: Horizontal(g0)
    c: Horizontal(g2)
    c: Vertical(g1)
    c: Vertical(g3)
    c: Coincident(g0,g-1)
    c: DistanceX(g2,g2) = 166
    c: DistanceY(g1,g1) = 90
FEATURE [PartDesign::Pad] Pad004  label="Pad-body"
  Direction = (0,0,1)
  Length = 5
  Length2 = 10
  Profile = -> Sketch004
  ReferenceAxis = -> Sketch004 [N_Axis]
  Type = 0
FEATURE [Sketcher::SketchObject] Sketch006
  ExternalGeometry = -> [Pad004]
  FullyConstrained = true
  MapMode = 5
  Placement = pos=(0,0,0) rot=(0.57735,-0.57735,-0.57735;2.0944rad)
  Support = -> [Pad004]
  sketch-geometry (1):
    g0: Circle CenterX=90 CenterY=2.5 CenterZ=0 NormalX=0 NormalY=0 NormalZ=1 AngleXU=0 Radius=4.5
  constraints (3):
    c: PointOnObject(g0,g-3)
    c: DistanceY(g-3,g0) = 2.5
    c: Diameter(g0) = 9
FEATURE [PartDesign::Pad] Pad006  label="Pad-slider_pin"
  BaseFeature = -> Pad004
  Direction = (-1,0,0)
  Length = 21
  Length2 = 177
  Profile = -> Sketch006
  ReferenceAxis = -> Sketch006 [N_Axis]
  Type = 4
FEATURE [Sketcher::SketchObject] Sketch016
  ExternalGeometry = -> [Pad006]
  FullyConstrained = true
  MapMode = 5
  Placement = pos=(0,0,0) rot=(1,0,0;3.14159rad)
  Support = -> [Pad006]
  sketch-geometry (10):
    g0: LineSegment StartX=15.25 StartY=10.5 StartZ=0 EndX=25.25 EndY=10.5 EndZ=0
    g1: LineSegment StartX=25.25 StartY=10.5 StartZ=0 EndX=25.25 EndY=-4.5 EndZ=0
    g2: LineSegment StartX=25.25 StartY=-4.5 StartZ=0 EndX=15.25 EndY=-4.5 EndZ=0
    g3: LineSegment StartX=15.25 StartY=-4.5 StartZ=0 EndX=15.25 EndY=10.5 EndZ=0
    g4: LineSegment StartX=140.75 StartY=10.5 StartZ=0 EndX=150.75 EndY=10.5 EndZ=0
    g5: LineSegment StartX=150.75 StartY=10.5 StartZ=0 EndX=150.75 EndY=-4.5 EndZ=0
    g6: LineSegment StartX=150.75 StartY=-4.5 StartZ=0 EndX=140.75 EndY=-4.5 EndZ=0
    g7: LineSegment StartX=140.75 StartY=-4.5 StartZ=0 EndX=140.75 EndY=10.5 EndZ=0
    g8: LineSegment StartX=0 StartY=0 StartZ=0 EndX=15.25 EndY=10.5 EndZ=0
    g9: LineSegment StartX=150.75 StartY=10.5 StartZ=0 EndX=166 EndY=-1.8e-15 EndZ=0
  constraints (28):
    c: Coincident(g0,g1)
    c: Coincident(g1,g2)
    c: Coincident(g2,g3)
    c: Coincident(g3,g0)
    c: Horizontal(g0)
    c: Horizontal(g2)
    c: Vertical(g1)
    c: Vertical(g3)
    c: Coincident(g4,g5)
    c: Coincident(g5,g6)
    c: Coincident(g6,g7)
    c: Coincident(g7,g4)
    c: Horizontal(g4)
    c: Horizontal(g6)
    c: Vertical(g5)
    c: Vertical(g7)
    c: Equal(g3,g7)
    c: Equal(g2,g6)
    c: DistanceY(g2,g-3) = 4.5
    c: DistanceX(g-3,g2) = 15.25
    c: DistanceX(g0,g0) = 10
    c: DistanceY(g1,g1) = 15
    c: Horizontal(g6,g1)
    c: Coincident(g8,g-3)
    c: Coincident(g8,g0)
    c: Coincident(g9,g4)
    c: Coincident(g9,g-3)
    c: Equal(g8,g9)
FEATURE [PartDesign::Pad] Pad009
  BaseFeature = -> Pad006
  Direction = (0,0,-1)
  Length = 7
  Length2 = 10
  Profile = -> Sketch016
  ReferenceAxis = -> Sketch016 [N_Axis]
  Type = 0
FEATURE [Sketcher::SketchObject] Sketch017
  FullyConstrained = true
  MapMode = 5
  Placement = pos=(15.25,0,0) rot=(0.57735,-0.57735,-0.57735;2.0944rad)
  Support = -> [Pad009]
  sketch-geometry (4):
    g0: Circle CenterX=-1 CenterY=-3.5 CenterZ=0 NormalX=0 NormalY=0 NormalZ=1 AngleXU=0 Radius=1.75
    g1: LineSegment StartX=10.5 StartY=0 StartZ=0 EndX=10.5 EndY=-7 EndZ=0
    g2: LineSegment StartX=10.5 StartY=-7 StartZ=0 EndX=3.5 EndY=-7 EndZ=0
    g3: LineSegment StartX=3.5 StartY=-7 StartZ=0 EndX=10.5 EndY=0 EndZ=0
  constraints (12):
    c: Diameter(g0) = 3.5
    c: DistanceY(g0,g-1) = 3.5
    c: DistanceX(g0,g-1) = 1
    c: PointOnObject(g1,g-1)
    c: Vertical(g1)
    c: Horizontal(g2)
    c: Coincident(g3,g1)
    c: Coincident(g2,g3)
    c: Coincident(g1,g2)
    c: Angle(g3,g1) = 0.785398
    c: DistanceX(g-1,g1) = 10.5
    c: DistanceY(g1,g1) = 7
FEATURE [PartDesign::Pocket] Pocket005
  BaseFeature = -> Pad009
  Direction = (1,0,0)
  Length = 5
  Length2 = 5
  Profile = -> Sketch017
  ReferenceAxis = -> Sketch017 [N_Axis]
  Type = 1
FEATURE [Sketcher::SketchObject] Sketch018
  ExternalGeometry = -> [Pocket005]
  FullyConstrained = true
  MapMode = 5
  Placement = pos=(-21,0,0) rot=(0.57735,-0.57735,-0.57735;2.0944rad)
  Support = -> [Pocket005]
  sketch-geometry (1):
    g0: GeomPoint X=90 Y=2.5 Z=0
  constraints (1):
    c: Coincident(g0,g-3)
FEATURE [PartDesign::Fillet] Fillet001
  Base = -> Pocket005 [Edge45,Edge23,Edge52,Edge28]
  BaseFeature = -> Pocket005
  Radius = 3.4
  SupportTransform = false
  UseAllEdges = false
FEATURE [Sketcher::SketchObject] Sketch062
  ExternalGeometry = -> [Fillet001]
  FullyConstrained = true
  MapMode = 5
  Placement = pos=(-21,0,0) rot=(0.57735,-0.57735,-0.57735;2.0944rad)
  Support = -> [Fillet001]
  sketch-geometry (2):
    g0: Circle CenterX=90 CenterY=2.5 CenterZ=0 NormalX=0 NormalY=0 NormalZ=1 AngleXU=0 Radius=3.95
    g1: Circle CenterX=90 CenterY=2.5 CenterZ=0 NormalX=0 NormalY=0 NormalZ=1 AngleXU=0 Radius=10
  constraints (4):
    c: Coincident(g0,g-3)
    c: Coincident(g1,g0)
    c: Diameter(g1) = 20
    c: Diameter(g0) = 7.9
FEATURE [PartDesign::Pocket] Pocket030  label="Pocket-bearing_shaft"
  BaseFeature = -> Fillet001
  Direction = (1,0,0)
  Length = 15
  Length2 = 5
  Profile = -> Sketch062
  ReferenceAxis = -> Sketch062 [N_Axis]
  Type = 0
FEATURE [Sketcher::SketchObject] Sketch063
  ExternalGeometry = -> [Pocket030]
  FullyConstrained = true
  MapMode = 5
  Placement = pos=(0,0,5) rot=(0,0,1;0rad)
  Support = -> [Pocket030]
  sketch-geometry (1):
    g0: Circle CenterX=-13.5 CenterY=-90 CenterZ=0 NormalX=0 NormalY=0 NormalZ=1 AngleXU=0 Radius=0.5
  constraints (3):
    c: Diameter(g0) = 1
    c: DistanceX(g0,g-3) = 13.5
    c: DistanceY(g-4,g0) = 4.5
FEATURE [PartDesign::Pocket] Pocket031
  BaseFeature = -> Pocket030
  Direction = (0,0,-1)
  Length = 10
  Length2 = 10
  Profile = -> Sketch063
  ReferenceAxis = -> Sketch063 [N_Axis]
  Type = 4
FEATURE [PartDesign::Chamfer] Chamfer001
  Angle = 45
  Base = -> Pocket031 [Edge16,Edge17,Edge19]
  BaseFeature = -> Pocket031
  ChamferType = 0
  FlipDirection = false
  Size = 3
  Size2 = 1
  SupportTransform = false
  UseAllEdges = false
FEATURE [Sketcher::SketchObject] Sketch069
  ExternalGeometry = -> [Chamfer001]
  FullyConstrained = true
  MapMode = 5
  Placement = pos=(-21,0,0) rot=(0.57735,-0.57735,-0.57735;2.0944rad)
  Support = -> [Chamfer001]
  sketch-geometry (1):
    g0: Circle CenterX=90 CenterY=2.5 CenterZ=0 NormalX=0 NormalY=0 NormalZ=1 AngleXU=0 Radius=6
  constraints (2):
    c: Coincident(g0,g-3)
    c: Diameter(g0) = 12
FEATURE [PartDesign::Pocket] Pocket035
  BaseFeature = -> Chamfer001
  Direction = (1,0,0)
  Length = 5
  Length2 = 5
  Profile = -> Sketch069
  ReferenceAxis = -> Sketch069 [N_Axis]
  Type = 0
FEATURE [Sketcher::SketchObject] Sketch108
  ExternalGeometry = -> [Pocket035]
  FullyConstrained = true
  MapMode = 5
  Placement = pos=(0,0,0) rot=(0.57735,-0.57735,-0.57735;2.0944rad)
  Support = -> [Pocket035]
  sketch-geometry (1):
    g0: Circle CenterX=90 CenterY=2.5 CenterZ=0 NormalX=0 NormalY=0 NormalZ=1 AngleXU=0 Radius=5.75
  constraints (2):
    c: Coincident(g0,g-3)
    c: Diameter(g0) = 11.5
FEATURE [PartDesign::Pad] Pad048
  BaseFeature = -> Pocket035
  Direction = (-1,0,0)
  Length = 166
  Length2 = 10
  Profile = -> Sketch108
  ReferenceAxis = -> Sketch108 [N_Axis]
  Reversed = true
  Type = 0
FEATURE [Sketcher::SketchObject] Sketch109
  ExternalGeometry = -> [Pad048]
  FullyConstrained = true
  MapMode = 5
  Placement = pos=(177,0,0) rot=(0.57735,0.57735,0.57735;2.0944rad)
  Support = -> [Pad048]
  sketch-geometry (2):
    g0: Circle CenterX=-90 CenterY=2.5 CenterZ=0 NormalX=0 NormalY=0 NormalZ=1 AngleXU=0 Radius=3.8
    g1: Circle CenterX=-90 CenterY=2.5 CenterZ=0 NormalX=0 NormalY=0 NormalZ=1 AngleXU=0 Radius=6
  constraints (4):
    c: Coincident(g0,g-3)
    c: Coincident(g1,g0)
    c: Diameter(g0) = 7.6
    c: Diameter(g1) = 12
FEATURE [PartDesign::Pocket] Pocket055
  BaseFeature = -> Pad048
  Direction = (-1,0,0)
  Length = 11
  Length2 = 5
  Profile = -> Sketch109
  ReferenceAxis = -> Sketch109 [N_Axis]
  Type = 0
FEATURE [Sketcher::SketchObject] Sketch110
  ExternalGeometry = -> [Pocket055]
  FullyConstrained = true
  MapMode = 5
  Placement = pos=(166,0,0) rot=(0.57735,0.57735,0.57735;2.0944rad)
  Support = -> [Pocket055]
  sketch-geometry (1):
    g0: Circle CenterX=-90 CenterY=2.5 CenterZ=0 NormalX=0 NormalY=0 NormalZ=1 AngleXU=0 Radius=4.5
  constraints (2):
    c: Coincident(g0,g-3)
    c: PointOnObject(g-3,g0)
FEATURE [PartDesign::Pad] Pad049  label="Pad-bearing_inside_retainer"
  BaseFeature = -> Pocket055
  Direction = (1,0,0)
  Length = 4.5
  Length2 = 10
  Profile = -> Sketch110
  ReferenceAxis = -> Sketch110 [N_Axis]
  Type = 0
FEATURE [Sketcher::SketchObject] Sketch113
  ExternalGeometry = -> [Pad049]
  FullyConstrained = true
  MapMode = 5
  Placement = pos=(177,0,0) rot=(0.57735,0.57735,0.57735;2.0944rad)
  Support = -> [Pad049]
  sketch-geometry (2):
    g0: GeomPoint X=-93.8 Y=2.5 Z=0
    g1: Circle CenterX=-90 CenterY=2.5 CenterZ=0 NormalX=0 NormalY=0 NormalZ=1 AngleXU=0 Radius=3.8
  constraints (4):
    c: PointOnObject(g0,g-3)
    c: Horizontal(g0,g-3)
    c: Coincident(g1,g-3)
    c: PointOnObject(g0,g1)
FEATURE [PartDesign::Pocket] Pocket056  label="Pocket-remove_bearing_shaft"
  BaseFeature = -> Pad049
  Direction = (-1,0,0)
  Length = 6.5
  Length2 = 5
  Profile = -> Sketch113
  ReferenceAxis = -> Sketch113 [N_Axis]
  Type = 0
FEATURE [Sketcher::SketchObject] Sketch114
  ExternalGeometry = -> [Pocket056]
  FullyConstrained = true
  MapMode = 5
  Placement = pos=(170.5,0,0) rot=(0.57735,0.57735,0.57735;2.0944rad)
  Support = -> [Pocket056]
  sketch-geometry (2):
    g0: GeomPoint X=-93.8 Y=2.5 Z=0
    g1: Circle CenterX=-90 CenterY=2.5 CenterZ=0 NormalX=0 NormalY=0 NormalZ=1 AngleXU=0 Radius=3.8
  constraints (4):
    c: PointOnObject(g0,g-3)
    c: Horizontal(g0,g-3)
    c: Coincident(g1,g-3)
    c: PointOnObject(g0,g1)
FEATURE [PartDesign::Pad] Pad051  label="Pad-bearing_shaft"
  BaseFeature = -> Pocket056
  Direction = (1,0,0)
  Length = 7.2
  Length2 = 10
  Profile = -> Sketch114
  ReferenceAxis = -> Sketch114 [N_Axis]
  Type = 0
FEATURE [Sketcher::SketchObject] Sketch115
  ExternalGeometry = -> [Pad051]
  FullyConstrained = true
  MapMode = 5
  Placement = pos=(177.7,0,0) rot=(0.57735,0.57735,0.57735;2.0944rad)
  Support = -> [Pad051]
  sketch-geometry (2):
    g0: GeomPoint X=-93.8 Y=2.5 Z=0
    g1: Circle CenterX=-90 CenterY=2.5 CenterZ=0 NormalX=0 NormalY=0 NormalZ=1 AngleXU=0 Radius=5.75
  constraints (4):
    c: PointOnObject(g0,g-3)
    c: Horizontal(g0,g-3)
    c: Coincident(g1,g-3)
    c: Diameter(g1) = 11.5
FEATURE [PartDesign::Pad] Pad052  label="Pad-bearing_retainer"
  BaseFeature = -> Pad051
  Direction = (1,0,0)
  Length = 2
  Length2 = 10
  Profile = -> Sketch115
  ReferenceAxis = -> Sketch115 [N_Axis]
  Type = 0
FEATURE [Sketcher::SketchObject] Sketch116
  ExternalGeometry = -> [Pad052]
  FullyConstrained = true
  MapMode = 5
  Placement = pos=(179.7,0,0) rot=(0.57735,0.57735,0.57735;2.0944rad)
  Support = -> [Pad052]
  sketch-geometry (1):
    g0: Circle CenterX=-90 CenterY=2.5 CenterZ=0 NormalX=0 NormalY=0 NormalZ=1 AngleXU=0 Radius=2.725
  constraints (2):
    c: Coincident(g0,g-3)
    c: Diameter(g0) = 5.45
FEATURE [PartDesign::Pocket] Pocket057  label="Pocket-screw_head"
  BaseFeature = -> Pad052
  Direction = (-1,0,0)
  Length = 2.9
  Length2 = 5
  Profile = -> Sketch116
  ReferenceAxis = -> Sketch116 [N_Axis]
  Type = 0
FEATURE [Sketcher::SketchObject] Sketch111
  ExternalGeometry = -> [Pocket055]
  FullyConstrained = true
  MapMode = 5
  Placement = pos=(166,0,0) rot=(0.57735,0.57735,0.57735;2.0944rad)
  Support = -> [Pocket057]
  sketch-geometry (10):
    g0: LineSegment StartX=-88.4123 StartY=5.25 StartZ=0 EndX=-91.5877 EndY=5.25 EndZ=0
    g1: LineSegment StartX=-91.5877 StartY=5.25 StartZ=0 EndX=-93.1754 EndY=2.5 EndZ=0
    g2: LineSegment StartX=-93.1754 StartY=2.5 StartZ=0 EndX=-91.5877 EndY=-0.25 EndZ=0
    g3: LineSegment StartX=-91.5877 StartY=-0.25 StartZ=0 EndX=-88.4123 EndY=-0.25 EndZ=0
    g4: LineSegment StartX=-88.4123 StartY=-0.25 StartZ=0 EndX=-86.8246 EndY=2.5 EndZ=0
    g5: LineSegment StartX=-86.8246 StartY=2.5 StartZ=0 EndX=-88.4123 EndY=5.25 EndZ=0
    g6: Circle CenterX=-90 CenterY=2.5 CenterZ=0 NormalX=0 NormalY=0 NormalZ=1 AngleXU=0 Radius=3.17543
    g7: LineSegment StartX=-91.5877 StartY=5.25 StartZ=0 EndX=-101.588 EndY=5.25 EndZ=0
    g8: LineSegment StartX=-101.588 StartY=5.25 StartZ=0 EndX=-101.588 EndY=-0.25 EndZ=0
    g9: LineSegment StartX=-101.588 StartY=-0.25 StartZ=0 EndX=-91.5877 EndY=-0.25 EndZ=0
  constraints (24):
    c: Coincident(g0,g1)
    c: Coincident(g1,g2)
    c: Coincident(g2,g3)
    c: Coincident(g3,g4)
    c: Coincident(g4,g5)
    c: Coincident(g5,g0)
    c: Equal(g0, g1-g5) x5
    c: PointOnObject(g0,g6)
    c: PointOnObject(g1,g6)
    c: PointOnObject(g2,g6)
    c: PointOnObject(g3,g6)
    c: PointOnObject(g4,g6)
    c: PointOnObject(g5,g6)
    c: Coincident(g6,g-3)
    c: Horizontal(g0)
    c: Coincident(g7,g0)
    c: Horizontal(g7)
    c: Coincident(g8,g7)
    c: Vertical(g8)
    c: Coincident(g9,g8)
    c: Coincident(g9,g2)
    c: Horizontal(g9)
    c: DistanceY(g8,g8) = 5.5
    c: DistanceX(g7,g7) = 10
FEATURE [PartDesign::Pocket] Pocket058  label="Pocket-nut_profile"
  BaseFeature = -> Pocket057
  Direction = (-1,0,0)
  Length = 9
  Length2 = 5
  Profile = -> Sketch111
  ReferenceAxis = -> Sketch111 [N_Axis]
  Type = 0
FEATURE [Sketcher::SketchObject] Sketch117
  ExternalGeometry = -> [Pocket058]
  FullyConstrained = true
  MapMode = 5
  Placement = pos=(166,0,0) rot=(0.57735,0.57735,0.57735;2.0944rad)
  Support = -> [Pocket058]
  sketch-geometry (1):
    g0: Circle CenterX=-90 CenterY=2.5 CenterZ=0 NormalX=0 NormalY=0 NormalZ=1 AngleXU=0 Radius=5.75
  constraints (2):
    c: Coincident(g0,g-3)
    c: PointOnObject(g-3,g0)
FEATURE [PartDesign::Pad] Pad053  label="Pad-bury nut profile"
  BaseFeature = -> Pocket058
  Direction = (1,0,0)
  Length = 4
  Length2 = 10
  Profile = -> Sketch117
  ReferenceAxis = -> Sketch117 [N_Axis]
  Reversed = true
  Type = 0
FEATURE [Sketcher::SketchObject] Sketch118
  ExternalGeometry = -> [Pad053]
  FullyConstrained = true
  MapMode = 5
  Placement = pos=(176.8,0,0) rot=(0.57735,0.57735,0.57735;2.0944rad)
  Support = -> [Pad053]
  sketch-geometry (1):
    g0: Circle CenterX=-90 CenterY=2.5 CenterZ=0 NormalX=0 NormalY=0 NormalZ=1 AngleXU=0 Radius=1.5
  constraints (2):
    c: Coincident(g0,g-3)
    c: Diameter(g0) = 3
FEATURE [PartDesign::Pocket] Pocket059
  BaseFeature = -> Pad053
  Direction = (-1,0,0)
  Length = 110
  Length2 = 5
  Profile = -> Sketch118
  ReferenceAxis = -> Sketch118 [N_Axis]
  Type = 0
FEATURE [Sketcher::SketchObject] Sketch124
  ExternalGeometry = -> [Pocket059]
  FullyConstrained = true
  MapMode = 5
  Placement = pos=(0,0,-0.25) rot=(0,0,1;0rad)
  Support = -> [Pocket059]
  sketch-geometry (3):
    g0: LineSegment StartX=157 StartY=-88.4123 StartZ=0 EndX=153.36 EndY=-98.4123 EndZ=0
    g1: LineSegment StartX=153.36 StartY=-98.4123 StartZ=0 EndX=157 EndY=-98.4123 EndZ=0
    g2: LineSegment StartX=157 StartY=-98.4123 StartZ=0 EndX=157 EndY=-88.4123 EndZ=0
  constraints (8):
    c: Coincident(g0,g-4)
    c: Coincident(g1,g0)
    c: Horizontal(g1)
    c: Coincident(g2,g1)
    c: Coincident(g2,g0)
    c: Vertical(g2)
    c: Angle(g0,g2) = 0.349066
    c: DistanceY(g2,g2) = 10
FEATURE [PartDesign::Pocket] Pocket062
  BaseFeature = -> Pocket059
  Direction = (0,0,-1)
  Length = 5.5
  Length2 = 5
  Profile = -> Sketch124
  ReferenceAxis = -> Sketch124 [N_Axis]
  Reversed = true
  Type = 0
FEATURE [PartDesign::Fillet] Fillet043
  Base = -> Pocket062 [Edge47,Edge77,Edge31,Edge54,Edge81,Edge80,Edge78]
  BaseFeature = -> Pocket062
  Radius = 0.5
  SupportTransform = false
  UseAllEdges = false
FEATURE [PartDesign::Fillet] Fillet044
  Base = -> Fillet043 [Edge11,Edge66]
  BaseFeature = -> Fillet043
  Radius = 0.3
  SupportTransform = false
  UseAllEdges = false
FEATURE [PartDesign::Fillet] Fillet045
  Base = -> Fillet044 [Edge104,Edge38]
  BaseFeature = -> Fillet044
  Radius = 0.3
  SupportTransform = false
  UseAllEdges = false
FEATURE [PartDesign::Body] Body003
  Group = -> [Sketch004,Pad004,Sketch006,Pad006,Sketch016,Pad009,Sketch017,Pocket005,Sketch018,Fillet001,Sketch062,Pocket030,Sketch063,Pocket031,Chamfer001,Sketch069,Pocket035,Sketch108,Pad048,Sketch109,Pocket055,Sketch110,Pad049,Sketch111,Sketch113,Pocket056,Sketch114,Pad051,Sketch115,Pad052,Sketch116,Pocket057,Pocket058,Sketch117,Pad053,Sketch118,Pocket059,Sketch124,Pocket062,Fillet043,Fillet044,Fillet045,+5 more]
  Origin = -> Origin003
  Placement = pos=(19.5211,29.3396,-3.97852) rot=(0.102719,-0.284327,-0.953209;2.07135rad)
  Tip = -> Pad057
COMPONENT P3 — recipe-attached ("Slide-mid-Body001", modeled in this document).
Construction recipe (the document's own serialized feature program — sketch geometry with constraints, then the solid features built on it; lengths are millimeters unless a unit is written):

FEATURE [Sketcher::SketchObject] Sketch019
  FullyConstrained = true
  MapMode = 5
  Placement = pos=(0,0,0) rot=(0.57735,0.57735,0.57735;2.0944rad)
  Support = -> [YZ_Plane004]
  sketch-geometry (4):
    g0: LineSegment StartX=0 StartY=0 StartZ=0 EndX=20 EndY=0 EndZ=0
    g1: LineSegment StartX=20 StartY=0 StartZ=0 EndX=20 EndY=30 EndZ=0
    g2: LineSegment StartX=20 StartY=30 StartZ=0 EndX=0 EndY=30 EndZ=0
    g3: LineSegment StartX=0 StartY=30 StartZ=0 EndX=0 EndY=0 EndZ=0
  constraints (11):
    c: Coincident(g0,g1)
    c: Coincident(g1,g2)
    c: Coincident(g2,g3)
    c: Coincident(g3,g0)
    c: Horizontal(g0)
    c: Horizontal(g2)
    c: Vertical(g1)
    c: Vertical(g3)
    c: Coincident(g0,g-1)
    c: DistanceY(g3,g3) = 30
    c: DistanceX(g0,g0) = 20
FEATURE [PartDesign::Pad] Pad010  label="Pad-body002"
  Direction = (1,-2e-16,3e-16)
  Length = 200
  Length2 = 10
  Placement = pos=(0,0,0) rot=(0.57735,0.57735,0.57735;2.0944rad)
  Profile = -> Sketch019
  ReferenceAxis = -> Sketch019 [N_Axis]
  Type = 0
FEATURE [Sketcher::SketchObject] Sketch020
  FullyConstrained = true
  MapMode = 5
  Placement = pos=(8.8e-15,20,-4.4e-15) rot=(0.57735,0.57735,0.57735;4.18879rad)
  Support = -> [Pad010]
  sketch-geometry (5):
    g0: Circle CenterX=15 CenterY=10 CenterZ=0 NormalX=0 NormalY=0 NormalZ=1 AngleXU=0 Radius=5
    g1: ArcOfCircle CenterX=15 CenterY=190 CenterZ=0 NormalX=0 NormalY=0 NormalZ=1 AngleXU=0 Radius=5 StartAngle=1.7e-15 EndAngle=3.14159
    g2: ArcOfCircle CenterX=15 CenterY=35 CenterZ=0 NormalX=0 NormalY=0 NormalZ=1 AngleXU=0 Radius=5 StartAngle=3.14159 EndAngle=6.28319
    g3: LineSegment StartX=10 StartY=190 StartZ=0 EndX=10 EndY=35 EndZ=0
    g4: LineSegment StartX=20 StartY=35 StartZ=0 EndX=20 EndY=190 EndZ=0
  constraints (13):
    c: Diameter(g0) = 10
    c: DistanceX(g-1,g0) = 15
    c: DistanceY(g-1,g0) = 10
    c: Tangent(g1,g3) = -1.5708
    c: Tangent(g3,g2) = -1.5708
    c: Tangent(g2,g4) = -1.5708
    c: Tangent(g4,g1) = -1.5708
    c: Equal(g1,g2)
    c: Vertical(g3)
    c: Radius(g2) = 5
    c: Vertical(g2,g0)
    c: DistanceY(g0,g2) = 25
    c: DistanceY(g0,g1) = 180
FEATURE [PartDesign::Pocket] Pocket006  label="Pocket-slider_guide001"
  BaseFeature = -> Pad010
  Direction = (-4e-16,-1,2e-16)
  Length = 5
  Length2 = 5
  Placement = pos=(0,0,0) rot=(0.57735,0.57735,0.57735;2.0944rad)
  Profile = -> Sketch020
  ReferenceAxis = -> Sketch020 [N_Axis]
  Type = 1
FEATURE [Sketcher::SketchObject] Sketch021
  FullyConstrained = true
  MapMode = 5
  Placement = pos=(-8.4e-15,1.32e-14,30) rot=(0,0,-1;1.5708rad)
  Support = -> [Pocket006]
  sketch-geometry (2):
    g0: Circle CenterX=-10 CenterY=50 CenterZ=0 NormalX=0 NormalY=0 NormalZ=1 AngleXU=0 Radius=5
    g1: Circle CenterX=-10 CenterY=180 CenterZ=0 NormalX=0 NormalY=0 NormalZ=1 AngleXU=0 Radius=5
  constraints (6):
    c: DistanceX(g0,g-1) = 10
    c: Vertical(g1,g0)
    c: DistanceY(g-1,g0) = 50
    c: DistanceY(g0,g1) = 130
    c: Diameter(g1) = 10
    c: Diameter(g0) = 10
FEATURE [PartDesign::Pocket] Pocket007  label="Pocket-mount_holes001"
  BaseFeature = -> Pocket006
  Direction = (7e-16,-7e-16,-1)
  Length = 28
  Length2 = 5
  Placement = pos=(0,0,0) rot=(0.57735,0.57735,0.57735;2.0944rad)
  Profile = -> Sketch021
  ReferenceAxis = -> Sketch021 [N_Axis]
  Type = 0
FEATURE [Sketcher::SketchObject] Sketch022  label="Sketch-slider_guide_line001"
  FullyConstrained = false
  MapMode = 5
  Placement = pos=(0,1e-16,0) rot=(-0.57735,-0.57735,0.57735;4.18879rad)
  Support = -> [Pocket007]
  sketch-geometry (1):
    g0: LineSegment StartX=-14.7121 StartY=24.4994 StartZ=0 EndX=-14.7121 EndY=187.74 EndZ=0
  constraints (1):
    c: Vertical(g0)
FEATURE [PartDesign::Body] Body004  label="Slide-mid-Body001"
  Group = -> [Sketch019,Pad010,Sketch020,Pocket006,Sketch021,Pocket007,Sketch022]
  Origin = -> Origin004
  Placement = pos=(-375,53,160) rot=(0,0,-1;1.5708rad)
  Tip = -> Pocket007
COMPONENT P4 — recipe-attached ("slicer", modeled in this document).
Construction recipe (the document's own serialized feature program — sketch geometry with constraints, then the solid features built on it; lengths are millimeters unless a unit is written):

FEATURE [Sketcher::SketchObject] Sketch033
  FullyConstrained = true
  MapMode = 5
  Support = -> [XY_Plane005]
  sketch-geometry (12):
    g0: LineSegment StartX=0 StartY=0 StartZ=0 EndX=80 EndY=0 EndZ=0
    g1: LineSegment StartX=80 StartY=0 StartZ=0 EndX=80 EndY=-200 EndZ=0
    g2: LineSegment StartX=80 StartY=-200 StartZ=0 EndX=0 EndY=-200 EndZ=0
    g3: LineSegment StartX=0 StartY=-200 StartZ=0 EndX=0 EndY=0 EndZ=0
    g4: LineSegment StartX=0 StartY=0 StartZ=0 EndX=10 EndY=20 EndZ=0
    g5: LineSegment StartX=10 StartY=20 StartZ=0 EndX=20 EndY=0 EndZ=0
    g6: LineSegment StartX=20 StartY=0 StartZ=0 EndX=30 EndY=20 EndZ=0
    g7: LineSegment StartX=30 StartY=20 StartZ=0 EndX=40 EndY=0 EndZ=0
    g8: LineSegment StartX=40 StartY=0 StartZ=0 EndX=50 EndY=20 EndZ=0
    g9: LineSegment StartX=50 StartY=20 StartZ=0 EndX=60 EndY=0 EndZ=0
    g10: LineSegment StartX=60 StartY=0 StartZ=0 EndX=70 EndY=20 EndZ=0
    g11: LineSegment StartX=70 StartY=20 StartZ=0 EndX=80 EndY=0 EndZ=0
  constraints (34):
    c: Coincident(g0,g1)
    c: Coincident(g1,g2)
    c: Coincident(g2,g3)
    c: Coincident(g3,g0)
    c: Horizontal(g0)
    c: Horizontal(g2)
    c: Vertical(g1)
    c: Vertical(g3)
    c: Coincident(g0,g-1)
    c: Coincident(g4,g0)
    c: Coincident(g5,g4)
    c: PointOnObject(g5,g0)
    c: Coincident(g6,g5)
    c: Coincident(g7,g6)
    c: PointOnObject(g7,g0)
    c: Coincident(g8,g7)
    c: Coincident(g9,g8)
    c: PointOnObject(g9,g0)
    c: Coincident(g10,g9)
    c: Coincident(g11,g10)
    c: Coincident(g11,g0)
    c: Horizontal(g4,g6)
    c: Horizontal(g6,g8)
    c: Horizontal(g8,g10)
    c: Equal(g4,g5)
    c: Equal(g5,g6)
    c: Equal(g6,g7)
    c: Equal(g7,g8)
    c: Equal(g8,g9)
    c: Equal(g9,g10)
    c: Equal(g10,g11)
    c: DistanceY(g3,g4) = 20
    c: DistanceX(g2,g2) = 80
    c: DistanceY(g3,g3) = 200
FEATURE [PartDesign::Pad] Pad012
  Direction = (0,0,1)
  Length = 100
  Length2 = 10
  Profile = -> Sketch033
  ReferenceAxis = -> Sketch033 [N_Axis]
  Type = 0
FEATURE [PartDesign::Body] Body006  label="slicer"
  Group = -> [Sketch033,Pad012]
  Origin = -> Origin005
  Placement = pos=(0,-118,0) rot=(0,0,1;0rad)
  Tip = -> Pad012
COMPONENT P5 — geometry summary ("slide_left"; no construction recipe available for this part):
  bounding box: 200.0 x 55.0 x 30.0 mm
  tessellated surface: 3,166 triangles
  volume: 72022 mm^3 (22% of its bounding box)
COMPONENT P6 — recipe-attached ("slicer001", modeled in this document).
Construction recipe (the document's own serialized feature program — sketch geometry with constraints, then the solid features built on it; lengths are millimeters unless a unit is written):

FEATURE [Sketcher::SketchObject] Sketch034
  FullyConstrained = true
  MapMode = 5
  Support = -> [XY_Plane007]
  sketch-geometry (12):
    g0: LineSegment StartX=0 StartY=0 StartZ=0 EndX=80 EndY=0 EndZ=0
    g1: LineSegment StartX=80 StartY=0 StartZ=0 EndX=80 EndY=-200 EndZ=0
    g2: LineSegment StartX=80 StartY=-200 StartZ=0 EndX=0 EndY=-200 EndZ=0
    g3: LineSegment StartX=0 StartY=-200 StartZ=0 EndX=0 EndY=0 EndZ=0
    g4: LineSegment StartX=0 StartY=0 StartZ=0 EndX=10 EndY=20 EndZ=0
    g5: LineSegment StartX=10 StartY=20 StartZ=0 EndX=20 EndY=0 EndZ=0
    g6: LineSegment StartX=20 StartY=0 StartZ=0 EndX=30 EndY=20 EndZ=0
    g7: LineSegment StartX=30 StartY=20 StartZ=0 EndX=40 EndY=0 EndZ=0
    g8: LineSegment StartX=40 StartY=0 StartZ=0 EndX=50 EndY=20 EndZ=0
    g9: LineSegment StartX=50 StartY=20 StartZ=0 EndX=60 EndY=0 EndZ=0
    g10: LineSegment StartX=60 StartY=0 StartZ=0 EndX=70 EndY=20 EndZ=0
    g11: LineSegment StartX=70 StartY=20 StartZ=0 EndX=80 EndY=0 EndZ=0
  constraints (34):
    c: Coincident(g0,g1)
    c: Coincident(g1,g2)
    c: Coincident(g2,g3)
    c: Coincident(g3,g0)
    c: Horizontal(g0)
    c: Horizontal(g2)
    c: Vertical(g1)
    c: Vertical(g3)
    c: Coincident(g0,g-1)
    c: Coincident(g4,g0)
    c: Coincident(g5,g4)
    c: PointOnObject(g5,g0)
    c: Coincident(g6,g5)
    c: Coincident(g7,g6)
    c: PointOnObject(g7,g0)
    c: Coincident(g8,g7)
    c: Coincident(g9,g8)
    c: PointOnObject(g9,g0)
    c: Coincident(g10,g9)
    c: Coincident(g11,g10)
    c: Coincident(g11,g0)
    c: Horizontal(g4,g6)
    c: Horizontal(g6,g8)
    c: Horizontal(g8,g10)
    c: Equal(g4,g5)
    c: Equal(g5,g6)
    c: Equal(g6,g7)
    c: Equal(g7,g8)
    c: Equal(g8,g9)
    c: Equal(g9,g10)
    c: Equal(g10,g11)
    c: DistanceY(g3,g4) = 20
    c: DistanceX(g2,g2) = 80
    c: DistanceY(g3,g3) = 200
FEATURE [PartDesign::Pad] Pad013
  Direction = (0,0,1)
  Length = 100
  Length2 = 10
  Profile = -> Sketch034
  ReferenceAxis = -> Sketch034 [N_Axis]
  Type = 0
FEATURE [PartDesign::Body] Body008  label="slicer001"
  Group = -> [Sketch034,Pad013]
  Origin = -> Origin007
  Placement = pos=(-375,-66.9999,160) rot=(0,0,-1;0rad)
  Tip = -> Pad013
COMPONENT P7 — recipe-attached ("slicer-door", modeled in this document).
Construction recipe (the document's own serialized feature program — sketch geometry with constraints, then the solid features built on it; lengths are millimeters unless a unit is written):

FEATURE [Sketcher::SketchObject] Sketch035
  FullyConstrained = true
  MapMode = 5
  Support = -> [XY_Plane008]
  sketch-geometry (12):
    g0: LineSegment StartX=0 StartY=0 StartZ=0 EndX=100 EndY=0 EndZ=0
    g1: LineSegment StartX=100 StartY=0 StartZ=0 EndX=100 EndY=-200 EndZ=0
    g2: LineSegment StartX=100 StartY=-200 StartZ=0 EndX=0 EndY=-200 EndZ=0
    g3: LineSegment StartX=0 StartY=-200 StartZ=0 EndX=0 EndY=0 EndZ=0
    g4: LineSegment StartX=0 StartY=0 StartZ=0 EndX=12.5 EndY=20 EndZ=0
    g5: LineSegment StartX=12.5 StartY=20 StartZ=0 EndX=25 EndY=0 EndZ=0
    g6: LineSegment StartX=25 StartY=0 StartZ=0 EndX=37.5 EndY=20 EndZ=0
    g7: LineSegment StartX=37.5 StartY=20 StartZ=0 EndX=50 EndY=0 EndZ=0
    g8: LineSegment StartX=50 StartY=0 StartZ=0 EndX=62.5 EndY=20 EndZ=0
    g9: LineSegment StartX=62.5 StartY=20 StartZ=0 EndX=75 EndY=0 EndZ=0
    g10: LineSegment StartX=75 StartY=0 StartZ=0 EndX=87.5 EndY=20 EndZ=0
    g11: LineSegment StartX=87.5 StartY=20 StartZ=0 EndX=100 EndY=0 EndZ=0
  constraints (34):
    c: Coincident(g0,g1)
    c: Coincident(g1,g2)
    c: Coincident(g2,g3)
    c: Coincident(g3,g0)
    c: Horizontal(g0)
    c: Horizontal(g2)
    c: Vertical(g1)
    c: Vertical(g3)
    c: Coincident(g0,g-1)
    c: Coincident(g4,g0)
    c: Coincident(g5,g4)
    c: PointOnObject(g5,g0)
    c: Coincident(g6,g5)
    c: Coincident(g7,g6)
    c: PointOnObject(g7,g0)
    c: Coincident(g8,g7)
    c: Coincident(g9,g8)
    c: PointOnObject(g9,g0)
    c: Coincident(g10,g9)
    c: Coincident(g11,g10)
    c: Coincident(g11,g0)
    c: Horizontal(g4,g6)
    c: Horizontal(g6,g8)
    c: Horizontal(g8,g10)
    c: Equal(g4,g5)
    c: Equal(g5,g6)
    c: Equal(g6,g7)
    c: Equal(g7,g8)
    c: Equal(g8,g9)
    c: Equal(g9,g10)
    c: Equal(g10,g11)
    c: DistanceY(g3,g4) = 20
    c: DistanceX(g2,g2) = 100
    c: DistanceY(g3,g3) = 200
FEATURE [PartDesign::Pad] Pad014
  Direction = (0,0,1)
  Length = 100
  Length2 = 10
  Profile = -> Sketch035
  ReferenceAxis = -> Sketch035 [N_Axis]
  Type = 0
FEATURE [PartDesign::Body] Body009  label="slicer-door"
  Group = -> [Sketch035,Pad014]
  Origin = -> Origin008
  Placement = pos=(-301,-38.5,136.994) rot=(-0.000109,-0.000109,1;1.5708rad)
  Tip = -> Pad014
COMPONENT P8 — recipe-attached ("slicer-door001", modeled in this document).
Construction recipe (the document's own serialized feature program — sketch geometry with constraints, then the solid features built on it; lengths are millimeters unless a unit is written):

FEATURE [Sketcher::SketchObject] Sketch036
  FullyConstrained = true
  MapMode = 5
  Support = -> [XY_Plane009]
  sketch-geometry (12):
    g0: LineSegment StartX=0 StartY=0 StartZ=0 EndX=100 EndY=0 EndZ=0
    g1: LineSegment StartX=100 StartY=0 StartZ=0 EndX=100 EndY=-200 EndZ=0
    g2: LineSegment StartX=100 StartY=-200 StartZ=0 EndX=0 EndY=-200 EndZ=0
    g3: LineSegment StartX=0 StartY=-200 StartZ=0 EndX=0 EndY=0 EndZ=0
    g4: LineSegment StartX=0 StartY=0 StartZ=0 EndX=12.5 EndY=20 EndZ=0
    g5: LineSegment StartX=12.5 StartY=20 StartZ=0 EndX=25 EndY=0 EndZ=0
    g6: LineSegment StartX=25 StartY=0 StartZ=0 EndX=37.5 EndY=20 EndZ=0
    g7: LineSegment StartX=37.5 StartY=20 StartZ=0 EndX=50 EndY=0 EndZ=0
    g8: LineSegment StartX=50 StartY=0 StartZ=0 EndX=62.5 EndY=20 EndZ=0
    g9: LineSegment StartX=62.5 StartY=20 StartZ=0 EndX=75 EndY=0 EndZ=0
    g10: LineSegment StartX=75 StartY=0 StartZ=0 EndX=87.5 EndY=20 EndZ=0
    g11: LineSegment StartX=87.5 StartY=20 StartZ=0 EndX=100 EndY=0 EndZ=0
  constraints (34):
    c: Coincident(g0,g1)
    c: Coincident(g1,g2)
    c: Coincident(g2,g3)
    c: Coincident(g3,g0)
    c: Horizontal(g0)
    c: Horizontal(g2)
    c: Vertical(g1)
    c: Vertical(g3)
    c: Coincident(g0,g-1)
    c: Coincident(g4,g0)
    c: Coincident(g5,g4)
    c: PointOnObject(g5,g0)
    c: Coincident(g6,g5)
    c: Coincident(g7,g6)
    c: PointOnObject(g7,g0)
    c: Coincident(g8,g7)
    c: Coincident(g9,g8)
    c: PointOnObject(g9,g0)
    c: Coincident(g10,g9)
    c: Coincident(g11,g10)
    c: Coincident(g11,g0)
    c: Horizontal(g4,g6)
    c: Horizontal(g6,g8)
    c: Horizontal(g8,g10)
    c: Equal(g4,g5)
    c: Equal(g5,g6)
    c: Equal(g6,g7)
    c: Equal(g7,g8)
    c: Equal(g8,g9)
    c: Equal(g9,g10)
    c: Equal(g10,g11)
    c: DistanceY(g3,g4) = 20
    c: DistanceX(g2,g2) = 100
    c: DistanceY(g3,g3) = 200
FEATURE [PartDesign::Pad] Pad015
  Direction = (0,0,1)
  Length = 100
  Length2 = 10
  Profile = -> Sketch036
  ReferenceAxis = -> Sketch036 [N_Axis]
  Type = 0
FEATURE [PartDesign::Body] Body010  label="slicer-door001"
  Group = -> [Sketch036,Pad015]
  Origin = -> Origin009
  Placement = pos=(-239.019,-38.5,137.008) rot=(-0.000109,-0.000109,1;1.5708rad)
  Tip = -> Pad015
COMPONENT P9 — recipe-attached ("slicer-door002", modeled in this document).
Construction recipe (the document's own serialized feature program — sketch geometry with constraints, then the solid features built on it; lengths are millimeters unless a unit is written):

FEATURE [Sketcher::SketchObject] Sketch037
  FullyConstrained = true
  MapMode = 5
  Support = -> [XY_Plane010]
  sketch-geometry (12):
    g0: LineSegment StartX=0 StartY=0 StartZ=0 EndX=100 EndY=0 EndZ=0
    g1: LineSegment StartX=100 StartY=0 StartZ=0 EndX=100 EndY=-200 EndZ=0
    g2: LineSegment StartX=100 StartY=-200 StartZ=0 EndX=0 EndY=-200 EndZ=0
    g3: LineSegment StartX=0 StartY=-200 StartZ=0 EndX=0 EndY=0 EndZ=0
    g4: LineSegment StartX=0 StartY=0 StartZ=0 EndX=12.5 EndY=20 EndZ=0
    g5: LineSegment StartX=12.5 StartY=20 StartZ=0 EndX=25 EndY=0 EndZ=0
    g6: LineSegment StartX=25 StartY=0 StartZ=0 EndX=37.5 EndY=20 EndZ=0
    g7: LineSegment StartX=37.5 StartY=20 StartZ=0 EndX=50 EndY=0 EndZ=0
    g8: LineSegment StartX=50 StartY=0 StartZ=0 EndX=62.5 EndY=20 EndZ=0
    g9: LineSegment StartX=62.5 StartY=20 StartZ=0 EndX=75 EndY=0 EndZ=0
    g10: LineSegment StartX=75 StartY=0 StartZ=0 EndX=87.5 EndY=20 EndZ=0
    g11: LineSegment StartX=87.5 StartY=20 StartZ=0 EndX=100 EndY=0 EndZ=0
  constraints (34):
    c: Coincident(g0,g1)
    c: Coincident(g1,g2)
    c: Coincident(g2,g3)
    c: Coincident(g3,g0)
    c: Horizontal(g0)
    c: Horizontal(g2)
    c: Vertical(g1)
    c: Vertical(g3)
    c: Coincident(g0,g-1)
    c: Coincident(g4,g0)
    c: Coincident(g5,g4)
    c: PointOnObject(g5,g0)
    c: Coincident(g6,g5)
    c: Coincident(g7,g6)
    c: PointOnObject(g7,g0)
    c: Coincident(g8,g7)
    c: Coincident(g9,g8)
    c: PointOnObject(g9,g0)
    c: Coincident(g10,g9)
    c: Coincident(g11,g10)
    c: Coincident(g11,g0)
    c: Horizontal(g4,g6)
    c: Horizontal(g6,g8)
    c: Horizontal(g8,g10)
    c: Equal(g4,g5)
    c: Equal(g5,g6)
    c: Equal(g6,g7)
    c: Equal(g7,g8)
    c: Equal(g8,g9)
    c: Equal(g9,g10)
    c: Equal(g10,g11)
    c: DistanceY(g3,g4) = 20
    c: DistanceX(g2,g2) = 100
    c: DistanceY(g3,g3) = 200
FEATURE [PartDesign::Pad] Pad016
  Direction = (0,0,1)
  Length = 100
  Length2 = 10
  Profile = -> Sketch037
  ReferenceAxis = -> Sketch037 [N_Axis]
  Type = 0
FEATURE [PartDesign::Body] Body011  label="slicer-door002"
  Group = -> [Sketch037,Pad016]
  Origin = -> Origin010
  Placement = pos=(61.2383,-95.0997,-36.5271) rot=(-0.000109,-0.000109,1;1.5708rad)
  Tip = -> Pad016
COMPONENT P10 — recipe-attached ("slicer-door003", modeled in this document).
Construction recipe (the document's own serialized feature program — sketch geometry with constraints, then the solid features built on it; lengths are millimeters unless a unit is written):

FEATURE [Sketcher::SketchObject] Sketch038
  FullyConstrained = true
  MapMode = 5
  Support = -> [XY_Plane011]
  sketch-geometry (12):
    g0: LineSegment StartX=0 StartY=0 StartZ=0 EndX=100 EndY=0 EndZ=0
    g1: LineSegment StartX=100 StartY=0 StartZ=0 EndX=100 EndY=-200 EndZ=0
    g2: LineSegment StartX=100 StartY=-200 StartZ=0 EndX=0 EndY=-200 EndZ=0
    g3: LineSegment StartX=0 StartY=-200 StartZ=0 EndX=0 EndY=0 EndZ=0
    g4: LineSegment StartX=0 StartY=0 StartZ=0 EndX=12.5 EndY=20 EndZ=0
    g5: LineSegment StartX=12.5 StartY=20 StartZ=0 EndX=25 EndY=0 EndZ=0
    g6: LineSegment StartX=25 StartY=0 StartZ=0 EndX=37.5 EndY=20 EndZ=0
    g7: LineSegment StartX=37.5 StartY=20 StartZ=0 EndX=50 EndY=0 EndZ=0
    g8: LineSegment StartX=50 StartY=0 StartZ=0 EndX=62.5 EndY=20 EndZ=0
    g9: LineSegment StartX=62.5 StartY=20 StartZ=0 EndX=75 EndY=0 EndZ=0
    g10: LineSegment StartX=75 StartY=0 StartZ=0 EndX=87.5 EndY=20 EndZ=0
    g11: LineSegment StartX=87.5 StartY=20 StartZ=0 EndX=100 EndY=0 EndZ=0
  constraints (34):
    c: Coincident(g0,g1)
    c: Coincident(g1,g2)
    c: Coincident(g2,g3)
    c: Coincident(g3,g0)
    c: Horizontal(g0)
    c: Horizontal(g2)
    c: Vertical(g1)
    c: Vertical(g3)
    c: Coincident(g0,g-1)
    c: Coincident(g4,g0)
    c: Coincident(g5,g4)
    c: PointOnObject(g5,g0)
    c: Coincident(g6,g5)
    c: Coincident(g7,g6)
    c: PointOnObject(g7,g0)
    c: Coincident(g8,g7)
    c: Coincident(g9,g8)
    c: PointOnObject(g9,g0)
    c: Coincident(g10,g9)
    c: Coincident(g11,g10)
    c: Coincident(g11,g0)
    c: Horizontal(g4,g6)
    c: Horizontal(g6,g8)
    c: Horizontal(g8,g10)
    c: Equal(g4,g5)
    c: Equal(g5,g6)
    c: Equal(g6,g7)
    c: Equal(g7,g8)
    c: Equal(g8,g9)
    c: Equal(g9,g10)
    c: Equal(g10,g11)
    c: DistanceY(g3,g4) = 20
    c: DistanceX(g2,g2) = 100
    c: DistanceY(g3,g3) = 200
FEATURE [PartDesign::Pad] Pad017
  Direction = (0,0,1)
  Length = 100
  Length2 = 10
  Profile = -> Sketch038
  ReferenceAxis = -> Sketch038 [N_Axis]
  Type = 0
FEATURE [PartDesign::Body] Body012  label="slicer-door003"
  Group = -> [Sketch038,Pad017]
  Origin = -> Origin011
  Placement = pos=(122.838,-95.0997,-36.5136) rot=(-0.000109,-0.000109,1;1.5708rad)
  Tip = -> Pad017
COMPONENT P11 — recipe-attached ("Slide-left-Body002", modeled in this document).
Construction recipe (the document's own serialized feature program — sketch geometry with constraints, then the solid features built on it; lengths are millimeters unless a unit is written):

FEATURE [Sketcher::SketchObject] Sketch039
  FullyConstrained = true
  MapMode = 5
  Placement = pos=(0,0,0) rot=(0.57735,0.57735,0.57735;2.0944rad)
  Support = -> [YZ_Plane012]
  sketch-geometry (4):
    g0: LineSegment StartX=0 StartY=0 StartZ=0 EndX=20 EndY=0 EndZ=0
    g1: LineSegment StartX=20 StartY=0 StartZ=0 EndX=20 EndY=30 EndZ=0
    g2: LineSegment StartX=20 StartY=30 StartZ=0 EndX=0 EndY=30 EndZ=0
    g3: LineSegment StartX=0 StartY=30 StartZ=0 EndX=0 EndY=0 EndZ=0
  constraints (11):
    c: Coincident(g0,g1)
    c: Coincident(g1,g2)
    c: Coincident(g2,g3)
    c: Coincident(g3,g0)
    c: Horizontal(g0)
    c: Horizontal(g2)
    c: Vertical(g1)
    c: Vertical(g3)
    c: Coincident(g0,g-1)
    c: DistanceY(g3,g3) = 30
    c: DistanceX(g0,g0) = 20
FEATURE [PartDesign::Pad] Pad018  label="Pad-body003"
  Direction = (1,-2e-16,3e-16)
  Length = 200
  Length2 = 10
  Placement = pos=(0,0,0) rot=(0.57735,0.57735,0.57735;2.0944rad)
  Profile = -> Sketch039
  ReferenceAxis = -> Sketch039 [N_Axis]
  Type = 0
FEATURE [Sketcher::SketchObject] Sketch040
  FullyConstrained = true
  MapMode = 5
  Placement = pos=(8.8e-15,20,-4.4e-15) rot=(0.57735,0.57735,0.57735;4.18879rad)
  Support = -> [Pad018]
  sketch-geometry (5):
    g0: Circle CenterX=15 CenterY=10 CenterZ=0 NormalX=0 NormalY=0 NormalZ=1 AngleXU=0 Radius=5
    g1: ArcOfCircle CenterX=15 CenterY=190 CenterZ=0 NormalX=0 NormalY=0 NormalZ=1 AngleXU=0 Radius=5 StartAngle=1.7e-15 EndAngle=3.14159
    g2: ArcOfCircle CenterX=15 CenterY=35 CenterZ=0 NormalX=0 NormalY=0 NormalZ=1 AngleXU=0 Radius=5 StartAngle=3.14159 EndAngle=6.28319
    g3: LineSegment StartX=10 StartY=190 StartZ=0 EndX=10 EndY=35 EndZ=0
    g4: LineSegment StartX=20 StartY=35 StartZ=0 EndX=20 EndY=190 EndZ=0
  constraints (13):
    c: Diameter(g0) = 10
    c: DistanceX(g-1,g0) = 15
    c: DistanceY(g-1,g0) = 10
    c: Tangent(g1,g3) = -1.5708
    c: Tangent(g3,g2) = -1.5708
    c: Tangent(g2,g4) = -1.5708
    c: Tangent(g4,g1) = -1.5708
    c: Equal(g1,g2)
    c: Vertical(g3)
    c: Radius(g2) = 5
    c: Vertical(g2,g0)
    c: DistanceY(g0,g2) = 25
    c: DistanceY(g0,g1) = 180
FEATURE [PartDesign::Pocket] Pocket015  label="Pocket-slider_guide002"
  BaseFeature = -> Pad018
  Direction = (-3e-16,-1,1e-16)
  Length = 5
  Length2 = 5
  Placement = pos=(0,0,0) rot=(0.57735,0.57735,0.57735;2.0944rad)
  Profile = -> Sketch040
  ReferenceAxis = -> Sketch040 [N_Axis]
  Type = 1
FEATURE [Sketcher::SketchObject] Sketch041
  FullyConstrained = true
  MapMode = 5
  Placement = pos=(-8.4e-15,1.32e-14,30) rot=(0,0,-1;1.5708rad)
  Support = -> [Pocket015]
  sketch-geometry (2):
    g0: Circle CenterX=-10 CenterY=50 CenterZ=0 NormalX=0 NormalY=0 NormalZ=1 AngleXU=0 Radius=3.1
    g1: Circle CenterX=-10 CenterY=180 CenterZ=0 NormalX=0 NormalY=0 NormalZ=1 AngleXU=0 Radius=3.1
  constraints (6):
    c: DistanceX(g0,g-1) = 10
    c: Vertical(g1,g0)
    c: DistanceY(g-1,g0) = 50
    c: DistanceY(g0,g1) = 130
    c: Diameter(g0) = 6.2
    c: Equal(g1,g0)
FEATURE [PartDesign::Pocket] Pocket016  label="Pocket-mount_holes002"
  BaseFeature = -> Pocket015
  Direction = (3e-16,-5e-16,-1)
  Length = 26.5
  Length2 = 5
  Placement = pos=(0,0,0) rot=(0.57735,0.57735,0.57735;2.0944rad)
  Profile = -> Sketch041
  ReferenceAxis = -> Sketch041 [N_Axis]
  Type = 0
FEATURE [Sketcher::SketchObject] Sketch042  label="Sketch-slider_guide_line002"
  FullyConstrained = false
  MapMode = 5
  Placement = pos=(0,1e-16,0) rot=(-0.57735,-0.57735,0.57735;4.18879rad)
  Support = -> [Pocket016]
  sketch-geometry (1):
    g0: LineSegment StartX=-14.7121 StartY=24.4994 StartZ=0 EndX=-14.7121 EndY=187.74 EndZ=0
  constraints (1):
    c: Vertical(g0)
FEATURE [Sketcher::SketchObject] Sketch043
  ExternalGeometry = -> [Pocket016]
  FullyConstrained = true
  MapMode = 5
  Placement = pos=(0,0,0) rot=(0.57735,0.57735,-0.57735;4.18879rad)
  Support = -> [Pocket016]
  sketch-geometry (8):
    g0: LineSegment StartX=-10 StartY=2.5 StartZ=0 EndX=-10 EndY=-52.5 EndZ=0
    g1: LineSegment StartX=0 StartY=0 StartZ=0 EndX=0 EndY=-30 EndZ=0
    g2: LineSegment StartX=0 StartY=-30 StartZ=0 EndX=20 EndY=-30 EndZ=0
    g3: GeomPoint X=0 Y=-15 Z=0
    g4: LineSegment StartX=4.24533 StartY=-52.5 StartZ=0 EndX=20 EndY=-30 EndZ=0
    g5: LineSegment StartX=-10 StartY=-52.5 StartZ=0 EndX=4.24533 EndY=-52.5 EndZ=0
    g6: LineSegment StartX=0 StartY=0 StartZ=0 EndX=-5 EndY=2.5 EndZ=0
    g7: LineSegment StartX=-5 StartY=2.5 StartZ=0 EndX=-10 EndY=2.5 EndZ=0
  constraints (20):
    c: Coincident(g6,g-4)
    c: Vertical(g0)
    c: Coincident(g5,g0)
    c: Coincident(g1,g6)
    c: Coincident(g0,g7)
    c: Coincident(g1,g2)
    c: Coincident(g1,g-4)
    c: DistanceX(g7,g6) = 10
    c: DistanceY(g0,g0) = 55
    c: PointOnObject(g3,g1)
    c: DistanceY(g3,g6) = 15
    c: DistanceY(g3,g7) = 17.5
    c: Horizontal(g5)
    c: Coincident(g5,g4)
    c: Coincident(g2,g4)
    c: Coincident(g2,g-3)
    c: Angle(g2,g4) = 0.959931
    c: Coincident(g6,g7)
    c: Horizontal(g7)
    c: DistanceX(g0,g6) = 5
FEATURE [PartDesign::Pad] Pad019
  BaseFeature = -> Pocket016
  Direction = (-1,2e-16,-2e-16)
  Length = 20
  Length2 = 10
  Placement = pos=(0,0,0) rot=(0.57735,0.57735,0.57735;2.0944rad)
  Profile = -> Sketch043
  ReferenceAxis = -> Sketch043 [N_Axis]
  Reversed = true
  Type = 0
FEATURE [Sketcher::SketchObject] Sketch044
  ExternalGeometry = -> [Pad019]
  FullyConstrained = true
  MapMode = 5
  Placement = pos=(-2.2e-15,-10,6e-16) rot=(-0.57735,-0.57735,0.57735;4.18879rad)
  Support = -> [Pad019]
  sketch-geometry (15):
    g0: Circle CenterX=-49.575 CenterY=14.9 CenterZ=0 NormalX=0 NormalY=0 NormalZ=1 AngleXU=0 Radius=1.125
    g1: Circle CenterX=-49.575 CenterY=5.1 CenterZ=0 NormalX=0 NormalY=0 NormalZ=1 AngleXU=0 Radius=1.125
    g2: Circle CenterX=-1.125 CenterY=14.9 CenterZ=0 NormalX=0 NormalY=0 NormalZ=1 AngleXU=0 Radius=1.125
    g3: Circle CenterX=-1.125 CenterY=5.1 CenterZ=0 NormalX=0 NormalY=0 NormalZ=1 AngleXU=0 Radius=1.125
    g4: LineSegment StartX=-46.35 StartY=0 StartZ=0 EndX=-4.35 EndY=0 EndZ=0
    g5: LineSegment StartX=-4.35 StartY=0 StartZ=0 EndX=-4.35 EndY=20 EndZ=0
    g6: LineSegment StartX=-4.35 StartY=20 StartZ=0 EndX=-46.35 EndY=20 EndZ=0
    g7: LineSegment StartX=-46.35 StartY=20 StartZ=0 EndX=-46.35 EndY=0 EndZ=0
    g8: LineSegment StartX=-49.575 StartY=14.9 StartZ=0 EndX=-49.575 EndY=5.1 EndZ=0
    g9: LineSegment StartX=-49.575 StartY=5.1 StartZ=0 EndX=-1.125 EndY=5.1 EndZ=0
    g10: LineSegment StartX=-1.125 StartY=14.9 StartZ=0 EndX=-49.575 EndY=14.9 EndZ=0
    g11: LineSegment StartX=-46.35 StartY=20 StartZ=0 EndX=-49.575 EndY=14.9 EndZ=0
    g12: LineSegment StartX=-4.35 StartY=20 StartZ=0 EndX=-1.125 EndY=14.9 EndZ=0
    g13: LineSegment StartX=-1.125 StartY=5.1 StartZ=0 EndX=-1.125 EndY=10 EndZ=0
    g14: LineSegment StartX=-1.125 StartY=10 StartZ=0 EndX=-1.125 EndY=14.9 EndZ=0
  constraints (39):
    c: Tangent(g3,g-2)
    c: Coincident(g4,g5)
    c: Coincident(g5,g6)
    c: Coincident(g6,g7)
    c: Coincident(g7,g4)
    c: Horizontal(g4)
    c: Horizontal(g6)
    c: Vertical(g5)
    c: Vertical(g7)
    c: Horizontal(g-4,g5)
    c: DistanceX(g6,g6) = 42
    c: Diameter(g2) = 2.25
    c: Equal(g0,g1)
    c: Equal(g1,g3)
    c: Equal(g3,g2)
    c: Coincident(g8,g0)
    c: Coincident(g8,g1)
    c: Vertical(g8)
    c: Coincident(g9,g1)
    c: Coincident(g9,g3)
    c: Horizontal(g9)
    c: Coincident(g13,g3)
    c: Coincident(g14,g2)
    c: Coincident(g10,g2)
    c: Coincident(g10,g0)
    c: Horizontal(g10)
    c: Coincident(g11,g6)
    c: Coincident(g11,g0)
    c: Coincident(g12,g5)
    c: Coincident(g12,g2)
    c: Equal(g12,g11)
    c: DistanceX(g9,g9) = 48.45
    c: DistanceY(g8,g8) = 9.8
    c: Coincident(g13,g14)
    c: Vertical(g13)
    c: Vertical(g14)
    c: Equal(g14,g13)
    c: DistanceY(g-4,g13) = 10
    c: PointOnObject(g4,g-5)
FEATURE [PartDesign::Pocket] Pocket017  label="Pocket-servo_mount_screw_hole_body_profile"
  BaseFeature = -> Pad019
  Direction = (1e-16,1,1e-16)
  Length = 10
  Length2 = 5
  Placement = pos=(0,0,0) rot=(0.57735,0.57735,0.57735;2.0944rad)
  Profile = -> Sketch044
  ReferenceAxis = -> Sketch044 [N_Axis]
  Type = 0
FEATURE [Sketcher::SketchObject] Sketch045
  ExternalGeometry = -> [Pocket017]
  FullyConstrained = true
  MapMode = 5
  Placement = pos=(-1.47e-14,0,52.5) rot=(0,0,-1;1.5708rad)
  Support = -> [Pocket017]
  sketch-geometry (4):
    g0: LineSegment StartX=-20 StartY=17.5 StartZ=0 EndX=5 EndY=17.5 EndZ=0
    g1: LineSegment StartX=5 StartY=17.5 StartZ=0 EndX=5 EndY=2.5 EndZ=0
    g2: LineSegment StartX=5 StartY=2.5 StartZ=0 EndX=-20 EndY=2.5 EndZ=0
    g3: LineSegment StartX=-20 StartY=2.5 StartZ=0 EndX=-20 EndY=17.5 EndZ=0
  constraints (12):
    c: Coincident(g0,g1)
    c: Coincident(g1,g2)
    c: Coincident(g2,g3)
    c: Coincident(g3,g0)
    c: Horizontal(g0)
    c: Horizontal(g2)
    c: Vertical(g1)
    c: Vertical(g3)
    c: DistanceX(g2,g2) = 25
    c: DistanceX(g1,g-3) = 5
    c: DistanceY(g-3,g1) = 2.5
    c: DistanceY(g0,g-4) = 2.5
FEATURE [PartDesign::Pocket] Pocket018  label="Pocket-servo_mount_top_nut_space"
  BaseFeature = -> Pocket017
  Direction = (3e-16,-1e-16,-1)
  Length = 6
  Length2 = 5
  Placement = pos=(0,0,0) rot=(0.57735,0.57735,0.57735;2.0944rad)
  Profile = -> Sketch045
  ReferenceAxis = -> Sketch045 [N_Axis]
  Type = 0
FEATURE [Sketcher::SketchObject] Sketch046
  ExternalGeometry = -> [Pocket018]
  FullyConstrained = true
  MapMode = 5
  Placement = pos=(7e-16,0,-2.5) rot=(0.707107,0.707107,0;3.14159rad)
  Support = -> [Pocket018]
  sketch-geometry (4):
    g0: LineSegment StartX=-5 StartY=17.5 StartZ=0 EndX=5 EndY=17.5 EndZ=0
    g1: LineSegment StartX=5 StartY=17.5 StartZ=0 EndX=5 EndY=2.5 EndZ=0
    g2: LineSegment StartX=5 StartY=2.5 StartZ=0 EndX=-5 EndY=2.5 EndZ=0
    g3: LineSegment StartX=-5 StartY=2.5 StartZ=0 EndX=-5 EndY=17.5 EndZ=0
  constraints (12):
    c: Coincident(g0,g1)
    c: Coincident(g1,g2)
    c: Coincident(g2,g3)
    c: Coincident(g3,g0)
    c: Horizontal(g0)
    c: Horizontal(g2)
    c: Vertical(g1)
    c: Vertical(g3)
    c: DistanceX(g-3,g2) = 5
    c: DistanceY(g-3,g2) = 2.5
    c: DistanceY(g0,g-3) = 2.5
    c: DistanceX(g0,g0) = 10
FEATURE [PartDesign::Pocket] Pocket019
  BaseFeature = -> Pocket018
  Direction = (-3e-16,1e-16,1)
  Length = 6
  Length2 = 5
  Placement = pos=(0,0,0) rot=(0.57735,0.57735,0.57735;2.0944rad)
  Profile = -> Sketch046
  ReferenceAxis = -> Sketch046 [N_Axis]
  Type = 0
FEATURE [Sketcher::SketchObject] Sketch047
  FullyConstrained = true
  MapMode = 5
  Placement = pos=(-8.4e-15,1.32e-14,30) rot=(0,0,-1;1.5708rad)
  Support = -> [Pocket019]
  sketch-geometry (8):
    g0: ArcOfCircle CenterX=-10 CenterY=40 CenterZ=0 NormalX=0 NormalY=0 NormalZ=1 AngleXU=0 Radius=6 StartAngle=3.14159 EndAngle=6.28319
    g1: ArcOfCircle CenterX=-10 CenterY=80 CenterZ=0 NormalX=0 NormalY=0 NormalZ=1 AngleXU=0 Radius=6 StartAngle=-1.8e-15 EndAngle=3.14159
    g2: LineSegment StartX=-4 StartY=40 StartZ=0 EndX=-4 EndY=80 EndZ=0
    g3: LineSegment StartX=-16 StartY=80 StartZ=0 EndX=-16 EndY=40 EndZ=0
    g4: ArcOfCircle CenterX=-10 CenterY=180 CenterZ=0 NormalX=0 NormalY=0 NormalZ=1 AngleXU=0 Radius=6 StartAngle=2.9e-15 EndAngle=3.14159
    g5: ArcOfCircle CenterX=-10 CenterY=140 CenterZ=0 NormalX=0 NormalY=0 NormalZ=1 AngleXU=0 Radius=6 StartAngle=3.14159 EndAngle=6.28319
    g6: LineSegment StartX=-16 StartY=180 StartZ=0 EndX=-16 EndY=140 EndZ=0
    g7: LineSegment StartX=-4 StartY=140 StartZ=0 EndX=-4 EndY=180 EndZ=0
  constraints (20):
    c: Tangent(g0,g2) = -1.5708
    c: Tangent(g2,g1) = -1.5708
    c: Tangent(g1,g3) = -1.5708
    c: Tangent(g3,g0) = -1.5708
    c: Equal(g0,g1)
    c: Vertical(g2)
    c: Diameter(g1) = 12
    c: DistanceY(g2,g2) = 40
    c: DistanceX(g-1,g0) = -10
    c: DistanceY(g-1,g0) = 40
    c: Tangent(g4,g6) = -1.5708
    c: Tangent(g6,g5) = -1.5708
    c: Tangent(g5,g7) = -1.5708
    c: Tangent(g7,g4) = -1.5708
    c: Equal(g4,g5)
    c: Vertical(g6)
    c: DistanceY(g1,g5) = 60
    c: DistanceY(g7,g7) = 40
    c: Diameter(g5) = 12
    c: Vertical(g5,g1)
FEATURE [PartDesign::Pocket] Pocket020  label="Pocket-mount_slots"
  BaseFeature = -> Pocket019
  Direction = (3e-16,-6e-16,-1)
  Length = 26.5
  Length2 = 5
  Placement = pos=(0,0,0) rot=(0.57735,0.57735,0.57735;2.0944rad)
  Profile = -> Sketch047
  ReferenceAxis = -> Sketch047 [N_Axis]
  Type = 0
FEATURE [Sketcher::SketchObject] Sketch048
  FullyConstrained = true
  MapMode = 5
  Placement = pos=(-8.4e-15,1.32e-14,30) rot=(0,0,-1;1.5708rad)
  Support = -> [Pocket020]
  sketch-geometry (4):
    g0: Circle CenterX=-10 CenterY=45 CenterZ=0 NormalX=0 NormalY=0 NormalZ=1 AngleXU=0 Radius=3.1
    g1: Circle CenterX=-10 CenterY=75 CenterZ=0 NormalX=0 NormalY=0 NormalZ=1 AngleXU=0 Radius=3.1
    g2: Circle CenterX=-10 CenterY=145 CenterZ=0 NormalX=0 NormalY=0 NormalZ=1 AngleXU=0 Radius=3.1
    g3: Circle CenterX=-10 CenterY=175 CenterZ=0 NormalX=0 NormalY=0 NormalZ=1 AngleXU=0 Radius=3.1
  constraints (12):
    c: Equal(g0,g1)
    c: Equal(g1,g2)
    c: Equal(g2,g3)
    c: Vertical(g3,g2)
    c: Vertical(g2,g1)
    c: Vertical(g1,g0)
    c: DistanceX(g0,g-1) = 10
    c: DistanceY(g-1,g0) = 45
    c: DistanceY(g0,g1) = 30
    c: DistanceY(g1,g2) = 70
    c: DistanceY(g2,g3) = 30
    c: Diameter(g2) = 6.2
FEATURE [PartDesign::Pocket] Pocket021  label="Pocket-mounting-holes"
  BaseFeature = -> Pocket020
  Direction = (3e-16,-7e-16,-1)
  Length = 5
  Length2 = 5
  Placement = pos=(0,0,0) rot=(0.57735,0.57735,0.57735;2.0944rad)
  Profile = -> Sketch048
  ReferenceAxis = -> Sketch048 [N_Axis]
  Type = 1
FEATURE [Sketcher::SketchObject] Sketch049
  ExternalGeometry = -> [Pocket021]
  FullyConstrained = true
  MapMode = 5
  Placement = pos=(-1.47e-14,0,52.5) rot=(0,0,-1;1.5708rad)
  Support = -> [Pocket021]
  sketch-geometry (6):
    g0: LineSegment StartX=10 StartY=11 StartZ=0 EndX=8 EndY=11 EndZ=0
    g1: LineSegment StartX=8 StartY=11 StartZ=0 EndX=8 EndY=9 EndZ=0
    g2: LineSegment StartX=8 StartY=9 StartZ=0 EndX=10 EndY=9 EndZ=0
    g3: LineSegment StartX=10 StartY=9 StartZ=0 EndX=10 EndY=11 EndZ=0
    g4: LineSegment StartX=10 StartY=20 StartZ=0 EndX=8 EndY=11 EndZ=0
    g5: LineSegment StartX=8 StartY=9 StartZ=0 EndX=10 EndY=-3.6e-15 EndZ=0
  constraints (16):
    c: Coincident(g0,g1)
    c: Coincident(g1,g2)
    c: Coincident(g2,g3)
    c: Coincident(g3,g0)
    c: Horizontal(g0)
    c: Horizontal(g2)
    c: Vertical(g1)
    c: Vertical(g3)
    c: PointOnObject(g0,g-3)
    c: DistanceX(g2,g2) = 2
    c: DistanceY(g1,g1) = 2
    c: Coincident(g4,g-3)
    c: Coincident(g4,g0)
    c: Coincident(g5,g1)
    c: Coincident(g5,g-3)
    c: Equal(g4,g5)
FEATURE [PartDesign::Pocket] Pocket022  label="Pocket-servo_bracket_cantilever_cutout"
  BaseFeature = -> Pocket021
  Direction = (3e-16,-3e-16,-1)
  Length = 5
  Length2 = 5
  Placement = pos=(0,0,0) rot=(0.57735,0.57735,0.57735;2.0944rad)
  Profile = -> Sketch049
  ReferenceAxis = -> Sketch049 [N_Axis]
  Type = 1
FEATURE [Sketcher::SketchObject] Sketch051
  ExternalGeometry = -> [Pocket022]
  FullyConstrained = true
  MapMode = 5
  Placement = pos=(-8.4e-15,1.32e-14,30) rot=(0,0,-1;1.5708rad)
  Support = -> [Pocket022]
  sketch-geometry (4):
    g0: LineSegment StartX=-20 StartY=200 StartZ=0 EndX=0 EndY=200 EndZ=0
    g1: LineSegment StartX=0 StartY=200 StartZ=0 EndX=0 EndY=20 EndZ=0
    g2: LineSegment StartX=0 StartY=20 StartZ=0 EndX=-20 EndY=20 EndZ=0
    g3: LineSegment StartX=-20 StartY=20 StartZ=0 EndX=-20 EndY=200 EndZ=0
  constraints (10):
    c: Coincident(g0,g1)
    c: Coincident(g1,g2)
    c: Coincident(g2,g3)
    c: Coincident(g3,g0)
    c: Horizontal(g0)
    c: Horizontal(g2)
    c: Vertical(g1)
    c: Vertical(g3)
    c: Coincident(g0,g-3)
    c: Coincident(g1,g-4)
FEATURE [PartDesign::Pocket] Pocket023  label="Pocket-remove_flat_rail"
  BaseFeature = -> Pocket022
  Direction = (3e-16,-8e-16,-1)
  Length = 22
  Length2 = 5
  Placement = pos=(0,0,0) rot=(0.57735,0.57735,0.57735;2.0944rad)
  Profile = -> Sketch051
  ReferenceAxis = -> Sketch051 [N_Axis]
  Type = 0
FEATURE [Sketcher::SketchObject] Sketch052
  ExternalGeometry = -> [Pocket023]
  FullyConstrained = true
  MapMode = 5
  Placement = pos=(0,1e-16,0) rot=(-0.57735,-0.57735,0.57735;4.18879rad)
  Support = -> [Pocket023]
  sketch-geometry (14):
    g0: LineSegment StartX=-8 StartY=20 StartZ=0 EndX=-92.8376 EndY=20 EndZ=0
    g1: LineSegment StartX=-92.8376 StartY=20 StartZ=0 EndX=-27.323 EndY=200 EndZ=0
    g2: LineSegment StartX=-8 StartY=200 StartZ=0 EndX=-27.323 EndY=200 EndZ=0
    g3: LineSegment StartX=-59.0924 StartY=25 StartZ=0 EndX=-8 EndY=165.375 EndZ=0
    g4: LineSegment StartX=-8 StartY=165.375 StartZ=0 EndX=-8 EndY=200 EndZ=0
    g5: LineSegment StartX=-59.0924 StartY=25 StartZ=0 EndX=-8 EndY=25 EndZ=0
    g6: ArcOfCircle CenterX=-73.1434 CenterY=30.2523 CenterZ=0 NormalX=0 NormalY=0 NormalZ=1 AngleXU=0 Radius=5 StartAngle=2.79253 EndAngle=5.93412
    g7: ArcOfCircle CenterX=-15 CenterY=190 CenterZ=0 NormalX=0 NormalY=0 NormalZ=1 AngleXU=0 Radius=5 StartAngle=5.93412 EndAngle=9.07571
    g8: LineSegment StartX=-68.445 StartY=28.5422 StartZ=0 EndX=-10.3015 EndY=188.29 EndZ=0
    g9: LineSegment StartX=-19.6985 StartY=191.71 StartZ=0 EndX=-77.8419 EndY=31.9624 EndZ=0
    g10: LineSegment StartX=-19.6985 StartY=191.71 StartZ=0 EndX=-29.0954 EndY=195.13 EndZ=0
    g11: GeomPoint X=-34.2429 Y=122.511 Z=0
    g12: LineSegment StartX=-34.2429 StartY=122.511 StartZ=0 EndX=-24.846 EndY=119.091 EndZ=0
    g13: LineSegment StartX=-8 StartY=25 StartZ=0 EndX=-8 EndY=20 EndZ=0
  constraints (37):
    c: Coincident(g0,g-3)
    c: Horizontal(g0)
    c: Coincident(g1,g0)
    c: Coincident(g2,g-3)
    c: Coincident(g2,g1)
    c: Horizontal(g2)
    c: Angle(g1,g2) = 1.91986
    c: Coincident(g4,g3)
    c: Coincident(g5,g3)
    c: PointOnObject(g5,g-3)
    c: Horizontal(g5)
    c: Parallel(g3,g1)
    c: Tangent(g6,g8) = -1.5708
    c: Tangent(g8,g7) = -1.5708
    c: Tangent(g7,g9) = -1.5708
    c: Tangent(g9,g6) = -1.5708
    c: Equal(g6,g7)
    c: Parallel(g9,g1)
    c: Diameter(g6) = 10
    c: Coincident(g10,g7)
    c: PointOnObject(g10,g1)
    c: Angle(g1,g10) = 1.5708
    c: Distance(g10) = 10
    c: DistanceY(g7,g2) = 10
    c: DistanceX(g7,g2) = 7
    c: Coincident(g4,g2)
    c: Vertical(g4)
    c: PointOnObject(g11,g8)
    c: Coincident(g12,g11)
    c: PointOnObject(g12,g3)
    c: Angle(g8,g12) = 1.5708
    c: Distance(g12,g7) = 70
    c: Distance(g12) = 10
    c: Coincident(g13,g5)
    c: Coincident(g13,g0)
    c: DistanceY(g13,g13) = 5
    c: Distance(g9) = 170
FEATURE [PartDesign::Pad] Pad021  label="Pad-ramp"
  BaseFeature = -> Pocket023
  Direction = (-8e-16,-1,1e-16)
  Length = 20
  Length2 = 10
  Placement = pos=(0,0,0) rot=(0.57735,0.57735,0.57735;2.0944rad)
  Profile = -> Sketch052
  ReferenceAxis = -> Sketch052 [N_Axis]
  Reversed = true
  Type = 0
FEATURE [Sketcher::SketchObject] Sketch053  label="sketch-slide-guide"
  ExternalGeometry = -> [Pad021]
  FullyConstrained = true
  MapMode = 5
  Placement = pos=(0,1.19e-14,0) rot=(-0.57735,-0.57735,0.57735;4.18879rad)
  Support = -> [Pad021]
  sketch-geometry (3):
    g0: LineSegment StartX=-73.1434 StartY=30.2523 StartZ=0 EndX=-15 EndY=190 EndZ=0
    g1: LineSegment StartX=-15 StartY=190 StartZ=0 EndX=-10.3015 EndY=188.29 EndZ=0
    g2: LineSegment StartX=-73.1434 StartY=30.2523 StartZ=0 EndX=-68.445 EndY=28.5422 EndZ=0
  constraints (8):
    c: Coincident(g1,g0)
    c: Coincident(g1,g-3)
    c: Coincident(g2,g0)
    c: Coincident(g2,g-3)
    c: Distance(g2) = 5
    c: Angle(g-3,g2) = 1.5708
    c: Angle(g1,g-3) = 1.5708
    c: Parallel(g0,g-3)
FEATURE [Sketcher::SketchObject] Sketch054
  ExternalGeometry = -> [Pad021]
  FullyConstrained = true
  MapMode = 5
  Placement = pos=(0,1.19e-14,0) rot=(-0.57735,-0.57735,0.57735;4.18879rad)
  Support = -> [Pad021]
  sketch-geometry (5):
    g0: LineSegment StartX=-92.8376 StartY=20 StartZ=0 EndX=-27.323 EndY=200 EndZ=0
    g1: LineSegment StartX=-27.323 StartY=200 StartZ=0 EndX=-8 EndY=200 EndZ=0
    g2: LineSegment StartX=-8 StartY=200 StartZ=0 EndX=-8 EndY=165.375 EndZ=0
    g3: LineSegment StartX=-8 StartY=165.375 StartZ=0 EndX=-60.9123 EndY=20 EndZ=0
    g4: LineSegment StartX=-60.9123 StartY=20 StartZ=0 EndX=-92.8376 EndY=20 EndZ=0
  constraints (11):
    c: Coincident(g0,g-4)
    c: Coincident(g0,g-5)
    c: Coincident(g1,g0)
    c: Coincident(g1,g-6)
    c: Coincident(g2,g1)
    c: Coincident(g2,g-7)
    c: Coincident(g3,g2)
    c: PointOnObject(g3,g-4)
    c: Coincident(g4,g3)
    c: Coincident(g4,g0)
    c: PointOnObject(g-7,g3)
FEATURE [PartDesign::Pocket] Pocket024  label="Pocket-skinny_ramp"
  BaseFeature = -> Pad021
  Direction = (8e-16,1,-1e-16)
  Length = 8
  Length2 = 5
  Placement = pos=(0,0,0) rot=(0.57735,0.57735,0.57735;2.0944rad)
  Profile = -> Sketch054
  ReferenceAxis = -> Sketch054 [N_Axis]
  Type = 0
FEATURE [Sketcher::SketchObject] Sketch055
  ExternalGeometry = -> [Pocket024]
  FullyConstrained = true
  MapMode = 5
  Placement = pos=(7.1e-15,8,-9e-16) rot=(-0.57735,-0.57735,0.57735;4.18879rad)
  Support = -> [Pocket024]
  sketch-geometry (4):
    g0: ArcOfCircle CenterX=-73.1434 CenterY=30.2523 CenterZ=0 NormalX=0 NormalY=0 NormalZ=1 AngleXU=0 Radius=11.1 StartAngle=2.79253 EndAngle=5.93412
    g1: ArcOfCircle CenterX=-15 CenterY=190 CenterZ=0 NormalX=0 NormalY=0 NormalZ=1 AngleXU=0 Radius=11.1 StartAngle=5.93412 EndAngle=9.07571
    g2: LineSegment StartX=-62.7128 StartY=26.4558 StartZ=0 EndX=-4.56941 EndY=186.204 EndZ=0
    g3: LineSegment StartX=-25.4306 StartY=193.796 StartZ=0 EndX=-83.574 EndY=34.0487 EndZ=0
  constraints (8):
    c: Tangent(g0,g2) = -1.5708
    c: Tangent(g2,g1) = -1.5708
    c: Tangent(g1,g3) = -1.5708
    c: Tangent(g3,g0) = -1.5708
    c: Equal(g0,g1)
    c: Coincident(g0,g-3)
    c: Coincident(g1,g-4)
    c: Diameter(g0) = 22.2
FEATURE [PartDesign::Pocket] Pocket025  label="Pocket-bearing_slot"
  BaseFeature = -> Pocket024
  Direction = (9e-16,1,0)
  Length = 7.5
  Length2 = 5
  Placement = pos=(0,0,0) rot=(0.57735,0.57735,0.57735;2.0944rad)
  Profile = -> Sketch055
  ReferenceAxis = -> Sketch055 [N_Axis]
  Type = 0
FEATURE [Sketcher::SketchObject] Sketch056
  ExternalGeometry = -> [Pocket025]
  FullyConstrained = false
  MapMode = 5
  Placement = pos=(0,-3e-16,0) rot=(0.57735,0.57735,-0.57735;2.0944rad)
  Support = -> [Pocket025]
  sketch-geometry (7):
    g0: LineSegment StartX=-42.35 StartY=4 StartZ=0 EndX=-22.35 EndY=4 EndZ=0
    g1: LineSegment StartX=-22.35 StartY=4 StartZ=0 EndX=-22.35 EndY=15.3962 EndZ=0
    g2: LineSegment StartX=-22.35 StartY=15.3962 StartZ=0 EndX=-42.35 EndY=4 EndZ=0
    g3: LineSegment StartX=-42.35 StartY=8.6038 StartZ=0 EndX=-42.35 EndY=20 EndZ=0
    g4: LineSegment StartX=-42.35 StartY=20 StartZ=0 EndX=-22.35 EndY=20 EndZ=0
    g5: LineSegment StartX=-22.35 StartY=20 StartZ=0 EndX=-42.35 EndY=8.6038 EndZ=0
    g6: LineSegment StartX=-38.346 StartY=6.28152 StartZ=0 EndX=-40.3263 EndY=9.75691 EndZ=0
  constraints (21):
    c: Horizontal(g0)
    c: Coincident(g1,g0)
    c: Vertical(g1)
    c: Coincident(g2,g1)
    c: Coincident(g2,g0)
    c: Vertical(g3)
    c: Coincident(g4,g3)
    c: Horizontal(g4)
    c: Coincident(g5,g4)
    c: Coincident(g5,g3)
    c: Parallel(g2,g5)
    c: DistanceY(g3,g-5) = 0
    c: DistanceY(g-3,g0) = 4
    c: PointOnObject(g6,g2)
    c: PointOnObject(g6,g5)
    c: Angle(g2,g6) = 1.5708
    c: Distance(g6) = 4
    c: DistanceX(g-5,g3) = 4
    c: DistanceX(g0,g0) = 20
    c: Vertical(g4,g1)
    c: Vertical(g3,g0)
FEATURE [PartDesign::Pocket] Pocket026  label="Pocket-truss"
  BaseFeature = -> Pocket025
  Direction = (9e-16,1,1e-16)
  Length = 5
  Length2 = 5
  Placement = pos=(0,0,0) rot=(0.57735,0.57735,0.57735;2.0944rad)
  Profile = -> Sketch056
  ReferenceAxis = -> Sketch056 [N_Axis]
  Type = 1
FEATURE [Sketcher::SketchObject] Sketch057
  ExternalGeometry = -> [Pocket026]
  FullyConstrained = true
  MapMode = 5
  Placement = pos=(2.7e-15,0,0) rot=(0.57735,0.57735,-0.57735;4.18879rad)
  Support = -> [Pocket026]
  sketch-geometry (5):
    g0: LineSegment StartX=4 StartY=-22.35 StartZ=0 EndX=16 EndY=-22.35 EndZ=0
    g1: LineSegment StartX=16 StartY=-22.35 StartZ=0 EndX=16 EndY=-30 EndZ=0
    g2: LineSegment StartX=16 StartY=-30 StartZ=0 EndX=7.35244 EndY=-42.35 EndZ=0
    g3: LineSegment StartX=7.35244 StartY=-42.35 StartZ=0 EndX=4 EndY=-42.35 EndZ=0
    g4: LineSegment StartX=4 StartY=-42.35 StartZ=0 EndX=4 EndY=-22.35 EndZ=0
  constraints (15):
    c: Horizontal(g0)
    c: Coincident(g1,g0)
    c: PointOnObject(g1,g-7)
    c: Vertical(g1)
    c: Coincident(g2,g1)
    c: Coincident(g3,g2)
    c: Horizontal(g3)
    c: Coincident(g4,g3)
    c: Coincident(g4,g0)
    c: Vertical(g4)
    c: DistanceX(g-7,g0) = 4
    c: DistanceX(g1,g-7) = 4
    c: DistanceY(g-3,g3) = 4
    c: DistanceY(g4,g4) = 20
    c: Parallel(g2,g-4)
FEATURE [PartDesign::Pocket] Pocket027  label="Pocket-truss2"
  BaseFeature = -> Pocket026
  Direction = (1,-1e-16,8e-16)
  Length = 20
  Length2 = 5
  Placement = pos=(0,0,0) rot=(0.57735,0.57735,0.57735;2.0944rad)
  Profile = -> Sketch057
  ReferenceAxis = -> Sketch057 [N_Axis]
  Type = 0
FEATURE [Sketcher::SketchObject] Sketch058
  ExternalGeometry = -> [Pocket027]
  FullyConstrained = true
  MapMode = 5
  Placement = pos=(200,-4.4e-14,4.4e-14) rot=(0.57735,0.57735,0.57735;2.0944rad)
  Support = -> [Pocket027]
  sketch-geometry (4):
    g0: LineSegment StartX=-4.26e-14 StartY=8 StartZ=0 EndX=20 EndY=8 EndZ=0
    g1: LineSegment StartX=20 StartY=8 StartZ=0 EndX=20 EndY=1.07e-14 EndZ=0
    g2: LineSegment StartX=20 StartY=1.07e-14 StartZ=0 EndX=-4.26e-14 EndY=1.07e-14 EndZ=0
    g3: LineSegment StartX=-4.26e-14 StartY=1.07e-14 StartZ=0 EndX=-4.26e-14 EndY=8 EndZ=0
  constraints (10):
    c: Coincident(g0,g1)
    c: Coincident(g1,g2)
    c: Coincident(g2,g3)
    c: Coincident(g3,g0)
    c: Horizontal(g0)
    c: Horizontal(g2)
    c: Vertical(g1)
    c: Vertical(g3)
    c: Coincident(g0,g-5)
    c: Coincident(g1,g-4)
FEATURE [PartDesign::Pad] Pad022  label="Pad-mount_extender"
  BaseFeature = -> Pocket027
  Direction = (1,-1e-16,8e-16)
  Length = 14
  Length2 = 10
  Placement = pos=(0,0,0) rot=(0.57735,0.57735,0.57735;2.0944rad)
  Profile = -> Sketch058
  ReferenceAxis = -> Sketch058 [N_Axis]
  Type = 0
FEATURE [Sketcher::SketchObject] Sketch059
  ExternalGeometry = -> [Pad022]
  FullyConstrained = true
  MapMode = 5
  Placement = pos=(-6.6e-15,-9e-16,8) rot=(0,0,-1;1.5708rad)
  Support = -> [Pad022]
  sketch-geometry (1):
    g0: Circle CenterX=-10 CenterY=207 CenterZ=0 NormalX=0 NormalY=0 NormalZ=1 AngleXU=0 Radius=6
  constraints (3):
    c: Diameter(g0) = 12
    c: DistanceX(g-3,g0) = 10
    c: DistanceY(g0,g-3) = 7
FEATURE [PartDesign::Pocket] Pocket028  label="Pocket-mount_extender_inset"
  BaseFeature = -> Pad022
  Direction = (8e-16,1e-16,-1)
  Length = 4.5
  Length2 = 5
  Placement = pos=(0,0,0) rot=(0.57735,0.57735,0.57735;2.0944rad)
  Profile = -> Sketch059
  ReferenceAxis = -> Sketch059 [N_Axis]
  Type = 0
FEATURE [Sketcher::SketchObject] Sketch060
  ExternalGeometry = -> [Pocket028]
  FullyConstrained = true
  MapMode = 5
  Placement = pos=(-6.6e-15,-9e-16,8) rot=(0,0,-1;1.5708rad)
  Support = -> [Pocket028]
  sketch-geometry (1):
    g0: Circle CenterX=-10 CenterY=207 CenterZ=0 NormalX=0 NormalY=0 NormalZ=1 AngleXU=0 Radius=3.1
  constraints (2):
    c: Coincident(g0,g-3)
    c: Diameter(g0) = 6.2
FEATURE [PartDesign::Pocket] Pocket029  label="Pocket-mount_extender_mount_hole"
  BaseFeature = -> Pocket028
  Direction = (8e-16,1e-16,-1)
  Length = 5
  Length2 = 5
  Placement = pos=(0,0,0) rot=(0.57735,0.57735,0.57735;2.0944rad)
  Profile = -> Sketch060
  ReferenceAxis = -> Sketch060 [N_Axis]
  Type = 1
FEATURE [Sketcher::SketchObject] Sketch064
  ExternalGeometry = -> [Pocket029]
  FullyConstrained = true
  MapMode = 5
  Placement = pos=(1.78e-14,20,-2.2e-15) rot=(0.57735,0.57735,0.57735;4.18879rad)
  Support = -> [Pocket029]
  sketch-geometry (5):
    g0: LineSegment StartX=27.427 StartY=112 StartZ=0 EndX=8 EndY=112 EndZ=0
    g1: LineSegment StartX=8 StartY=102 StartZ=0 EndX=31.0667 EndY=102 EndZ=0
    g2: LineSegment StartX=31.0667 StartY=102 StartZ=0 EndX=27.427 EndY=112 EndZ=0
    g3: LineSegment StartX=8 StartY=112 StartZ=0 EndX=8 EndY=102 EndZ=0
    g4: GeomPoint X=8 Y=107 Z=0
  constraints (13):
    c: PointOnObject(g0,g-3)
    c: PointOnObject(g0,g-4)
    c: Horizontal(g0)
    c: PointOnObject(g1,g-4)
    c: PointOnObject(g1,g-3)
    c: Horizontal(g1)
    c: Coincident(g2,g1)
    c: Coincident(g2,g0)
    c: Coincident(g3,g0)
    c: Coincident(g3,g1)
    c: DistanceY(g3,g3) = 10
    c: Symmetric(g3,g3,g4)
    c: DistanceY(g-1,g4) = 107
FEATURE [PartDesign::Body] Body013  label="Slide-left-Body002"
  Group = -> [Sketch039,Pad018,Sketch040,Pocket015,Sketch041,Pocket016,Sketch042,Sketch043,Pad019,Sketch044,Pocket017,Sketch045,Pocket018,Sketch046,Pocket019,Sketch047,Pocket020,Sketch048,Pocket021,Sketch049,Pocket022,Sketch051,Pocket023,Sketch052,Pad021,Sketch053,Sketch054,Pocket024,Sketch055,Pocket025,Sketch056,Pocket026,Sketch057,Pocket027,Sketch058,Pad022,Sketch059,Pocket028,Sketch060,Pocket029,Sketch064,+60 more]
  Origin = -> Origin012
  Placement = pos=(-375,53,160) rot=(0,0,-1;1.5708rad)
  Tip = -> Fillet131
COMPONENT P12 — recipe-attached ("slicer002", modeled in this document).
Construction recipe (the document's own serialized feature program — sketch geometry with constraints, then the solid features built on it; lengths are millimeters unless a unit is written):

FEATURE [Sketcher::SketchObject] Sketch050
  FullyConstrained = true
  MapMode = 5
  Support = -> [XY_Plane013]
  sketch-geometry (12):
    g0: LineSegment StartX=0 StartY=0 StartZ=0 EndX=40 EndY=0 EndZ=0
    g1: LineSegment StartX=40 StartY=0 StartZ=0 EndX=40 EndY=-104 EndZ=0
    g2: LineSegment StartX=40 StartY=-104 StartZ=0 EndX=0 EndY=-104 EndZ=0
    g3: LineSegment StartX=0 StartY=-104 StartZ=0 EndX=0 EndY=0 EndZ=0
    g4: LineSegment StartX=0 StartY=0 StartZ=0 EndX=5 EndY=6 EndZ=0
    g5: LineSegment StartX=5 StartY=6 StartZ=0 EndX=10 EndY=0 EndZ=0
    g6: LineSegment StartX=10 StartY=0 StartZ=0 EndX=15 EndY=6 EndZ=0
    g7: LineSegment StartX=15 StartY=6 StartZ=0 EndX=20 EndY=0 EndZ=0
    g8: LineSegment StartX=20 StartY=0 StartZ=0 EndX=25 EndY=6 EndZ=0
    g9: LineSegment StartX=25 StartY=6 StartZ=0 EndX=30 EndY=0 EndZ=0
    g10: LineSegment StartX=30 StartY=0 StartZ=0 EndX=35 EndY=6 EndZ=0
    g11: LineSegment StartX=35 StartY=6 StartZ=0 EndX=40 EndY=0 EndZ=0
  constraints (34):
    c: Coincident(g0,g1)
    c: Coincident(g1,g2)
    c: Coincident(g2,g3)
    c: Coincident(g3,g0)
    c: Horizontal(g0)
    c: Horizontal(g2)
    c: Vertical(g1)
    c: Vertical(g3)
    c: Coincident(g0,g-1)
    c: Coincident(g4,g0)
    c: Coincident(g5,g4)
    c: PointOnObject(g5,g0)
    c: Coincident(g6,g5)
    c: Coincident(g7,g6)
    c: PointOnObject(g7,g0)
    c: Coincident(g8,g7)
    c: Coincident(g9,g8)
    c: PointOnObject(g9,g0)
    c: Coincident(g10,g9)
    c: Coincident(g11,g10)
    c: Coincident(g11,g0)
    c: Horizontal(g4,g6)
    c: Horizontal(g6,g8)
    c: Horizontal(g8,g10)
    c: Equal(g4,g5)
    c: Equal(g5,g6)
    c: Equal(g6,g7)
    c: Equal(g7,g8)
    c: Equal(g8,g9)
    c: Equal(g9,g10)
    c: Equal(g10,g11)
    c: DistanceY(g3,g4) = 6
    c: DistanceY(g3,g3) = 104
    c: DistanceX(g2,g2) = 40
FEATURE [PartDesign::Pad] Pad020
  Direction = (0,0,1)
  Length = 100
  Length2 = 10
  Profile = -> Sketch050
  ReferenceAxis = -> Sketch050 [N_Axis]
  Type = 0
FEATURE [PartDesign::Body] Body014  label="slicer002"
  Group = -> [Sketch050,Pad020]
  Origin = -> Origin013
  Placement = pos=(-377,-57,160) rot=(3e-06,0,-1;0rad)
  Tip = -> Pad020
COMPONENT P13 — recipe-attached ("Body-bearing", modeled in this document).
Construction recipe (the document's own serialized feature program — sketch geometry with constraints, then the solid features built on it; lengths are millimeters unless a unit is written):

FEATURE [Sketcher::SketchObject] Sketch061
  FullyConstrained = true
  MapMode = 5
  Support = -> [XY_Plane014]
  sketch-geometry (2):
    g0: Circle CenterX=0 CenterY=0 CenterZ=0 NormalX=0 NormalY=0 NormalZ=1 AngleXU=0 Radius=3.95
    g1: Circle CenterX=0 CenterY=0 CenterZ=0 NormalX=0 NormalY=0 NormalZ=1 AngleXU=0 Radius=11
  constraints (4):
    c: Coincident(g0,g-1)
    c: Coincident(g1,g0)
    c: Diameter(g0) = 7.9
    c: Diameter(g1) = 22
FEATURE [PartDesign::Pad] Pad023
  Direction = (0,0,1)
  Length = 7
  Length2 = 10
  Profile = -> Sketch061
  ReferenceAxis = -> Sketch061 [N_Axis]
  Type = 0
FEATURE [PartDesign::Body] Body015  label="Body-bearing"
  Group = -> [Sketch061,Pad023]
  Origin = -> Origin014
  Tip = -> Pad023
COMPONENT P14 — recipe-attached ("Body-v3_slicer", modeled in this document).
Construction recipe (the document's own serialized feature program — sketch geometry with constraints, then the solid features built on it; lengths are millimeters unless a unit is written):

FEATURE [Sketcher::SketchObject] Sketch072
  FullyConstrained = true
  MapMode = 5
  Placement = pos=(0,0,0) rot=(1,0,0;1.5708rad)
  Support = -> [XZ_Plane015]
  sketch-geometry (16):
    g0: LineSegment StartX=-3.8476e-12 StartY=-10.8333 StartZ=0 EndX=4 EndY=-10.8333 EndZ=0
    g1: LineSegment StartX=4 StartY=-10.8333 StartZ=0 EndX=4 EndY=-0.833334 EndZ=0
    g2: LineSegment StartX=4 StartY=-0.833334 StartZ=0 EndX=-15 EndY=-0.833334 EndZ=0
    g3: LineSegment StartX=-15 StartY=-0.833334 StartZ=0 EndX=-15 EndY=0.833334 EndZ=0
    g4: LineSegment StartX=-15 StartY=0.833334 StartZ=0 EndX=4 EndY=0.833334 EndZ=0
    g5: LineSegment StartX=4 StartY=0.833334 StartZ=0 EndX=4 EndY=10.8333 EndZ=0
    g6: LineSegment StartX=4 StartY=10.8333 StartZ=0 EndX=0 EndY=10.8333 EndZ=0
    g7: LineSegment StartX=0 StartY=10.8333 StartZ=0 EndX=0 EndY=0.853333 EndZ=0
    g8: LineSegment StartX=0 StartY=0.853333 StartZ=0 EndX=-19 EndY=0.853333 EndZ=0
    g9: LineSegment StartX=-19 StartY=0.853333 StartZ=0 EndX=-19 EndY=-0.853333 EndZ=0
    g10: LineSegment StartX=-19 StartY=-0.853333 StartZ=0 EndX=-3.8476e-12 EndY=-0.853333 EndZ=0
    g11: LineSegment StartX=-3.8476e-12 StartY=-0.853333 StartZ=0 EndX=-3.8476e-12 EndY=-10.8333 EndZ=0
    g12: LineSegment StartX=-19 StartY=0.853333 StartZ=0 EndX=-15 EndY=-0.833334 EndZ=0
    g13: LineSegment StartX=-15 StartY=0.833334 StartZ=0 EndX=-19 EndY=-0.853333 EndZ=0
    g14: LineSegment StartX=0 StartY=0.853333 StartZ=0 EndX=0 EndY=0 EndZ=0
    g15: LineSegment StartX=0 StartY=0 StartZ=0 EndX=-3.8476e-12 EndY=-0.853333 EndZ=0
  constraints (44):
    c: Horizontal(g0)
    c: Coincident(g1,g0)
    c: Vertical(g1)
    c: Coincident(g2,g1)
    c: Horizontal(g2)
    c: Coincident(g3,g2)
    c: Vertical(g3)
    c: Horizontal(g4)
    c: Coincident(g5,g4)
    c: Vertical(g5)
    c: Coincident(g6,g5)
    c: PointOnObject(g6,g-2)
    c: Horizontal(g6)
    c: Coincident(g7,g6)
    c: Vertical(g7)
    c: Coincident(g8,g7)
    c: Horizontal(g8)
    c: Coincident(g9,g8)
    c: Vertical(g9)
    c: Coincident(g10,g9)
    c: Horizontal(g10)
    c: Coincident(g11,g10)
    c: Vertical(g11)
    c: DistanceY(g3,g3) = 1.66667
    c: Coincident(g3,g4)
    c: DistanceY(g9,g9) = 1.70667
    c: Coincident(g12,g8)
    c: Coincident(g12,g2)
    c: Coincident(g13,g3)
    c: Coincident(g13,g9)
    c: Equal(g13,g12)
    c: DistanceX(g9,g2) = 4
    c: DistanceX(g0,g0) = 4
    c: Equal(g0,g6)
    c: Equal(g1,g5)
    c: DistanceY(g1,g1) = 10
    c: DistanceX(g2,g10) = 15
    c: Coincident(g11,g0)
    c: Vertical(g1,g4)
    c: Coincident(g14,g7)
    c: Coincident(g14,g-1)
    c: Coincident(g15,g14)
    c: Coincident(g15,g10)
    c: Equal(g15,g14)
FEATURE [PartDesign::Pad] Pad027  label="Pad-main_body"
  Direction = (0,-1,-2e-16)
  Length = 150
  Length2 = 10
  Placement = pos=(0,0,0) rot=(1,0,0;1.5708rad)
  Profile = -> Sketch072
  ReferenceAxis = -> Sketch072 [N_Axis]
  Type = 0
FEATURE [Sketcher::SketchObject] Sketch073
  ExternalGeometry = -> [Pad027]
  FullyConstrained = true
  MapMode = 5
  Placement = pos=(0,2e-16,0.853333) rot=(0,0,1;3.14159rad)
  Support = -> [Pad027]
  sketch-geometry (14):
    g0: ArcOfCircle CenterX=5.5 CenterY=50 CenterZ=0 NormalX=0 NormalY=0 NormalZ=1 AngleXU=0 Radius=1.7 StartAngle=1.5708 EndAngle=4.71239
    g1: ArcOfCircle CenterX=11.5 CenterY=50 CenterZ=0 NormalX=0 NormalY=0 NormalZ=1 AngleXU=0 Radius=1.7 StartAngle=4.71239 EndAngle=7.85398
    g2: LineSegment StartX=5.5 StartY=48.3 StartZ=0 EndX=11.5 EndY=48.3 EndZ=0
    g3: LineSegment StartX=11.5 StartY=51.7 StartZ=0 EndX=5.5 EndY=51.7 EndZ=0
    g4: ArcOfCircle CenterX=5.5 CenterY=75 CenterZ=0 NormalX=0 NormalY=0 NormalZ=1 AngleXU=0 Radius=1.7 StartAngle=1.5708 EndAngle=4.71239
    g5: ArcOfCircle CenterX=11.5 CenterY=75 CenterZ=0 NormalX=0 NormalY=0 NormalZ=1 AngleXU=0 Radius=1.7 StartAngle=4.71239 EndAngle=7.85398
    g6: LineSegment StartX=5.5 StartY=73.3 StartZ=0 EndX=11.5 EndY=73.3 EndZ=0
    g7: LineSegment StartX=11.5 StartY=76.7 StartZ=0 EndX=5.5 EndY=76.7 EndZ=0
    g8: ArcOfCircle CenterX=5.5 CenterY=100 CenterZ=0 NormalX=0 NormalY=0 NormalZ=1 AngleXU=0 Radius=1.7 StartAngle=1.5708 EndAngle=4.71239
    g9: ArcOfCircle CenterX=11.5 CenterY=100 CenterZ=0 NormalX=0 NormalY=0 NormalZ=1 AngleXU=0 Radius=1.7 StartAngle=4.71239 EndAngle=7.85398
    g10: LineSegment StartX=5.5 StartY=98.3 StartZ=0 EndX=11.5 EndY=98.3 EndZ=0
    g11: LineSegment StartX=11.5 StartY=101.7 StartZ=0 EndX=5.5 EndY=101.7 EndZ=0
    g12: LineSegment StartX=11.5 StartY=100 StartZ=0 EndX=11.5 EndY=75 EndZ=0
    g13: LineSegment StartX=11.5 StartY=75 StartZ=0 EndX=11.5 EndY=50 EndZ=0
  constraints (34):
    c: Tangent(g0,g2) = -1.5708
    c: Tangent(g2,g1) = -1.5708
    c: Tangent(g1,g3) = -1.5708
    c: Tangent(g3,g0) = -1.5708
    c: Equal(g0,g1)
    c: Horizontal(g2)
    c: Diameter(g1) = 3.4
    c: DistanceX(g2,g2) = 6
    c: DistanceX(g1,g-3) = 7.5
    c: DistanceY(g-3,g1) = 50
    c: Tangent(g4,g6) = -1.5708
    c: Tangent(g6,g5) = -1.5708
    c: Tangent(g5,g7) = -1.5708
    c: Tangent(g7,g4) = -1.5708
    c: Equal(g4,g5)
    c: Tangent(g8,g10) = -1.5708
    c: Tangent(g10,g9) = -1.5708
    c: Tangent(g9,g11) = -1.5708
    c: Tangent(g11,g8) = -1.5708
    c: Equal(g8,g9)
    c: Equal(g9,g5)
    c: Equal(g5,g1)
    c: Horizontal(g5,g4)
    c: Horizontal(g9,g8)
    c: Vertical(g8,g4)
    c: Vertical(g4,g0)
    c: Coincident(g12,g9)
    c: Coincident(g12,g5)
    c: Vertical(g12)
    c: Coincident(g13,g5)
    c: Coincident(g13,g1)
    c: Vertical(g13)
    c: Equal(g12,g13)
    c: DistanceY(g12,g12) = 25
FEATURE [PartDesign::Pad] Pad028  label="Pad-slots"
  BaseFeature = -> Pad027
  Direction = (0,-2e-16,1)
  Length = 10
  Length2 = 10
  Placement = pos=(0,0,0) rot=(1,0,0;1.5708rad)
  Profile = -> Sketch073
  ReferenceAxis = -> Sketch073 [N_Axis]
  Type = 0
FEATURE [PartDesign::Mirrored] Mirrored  label="Mirrored-slots_top_to_bottom"
  BaseFeature = -> Pad028
  MirrorPlane = -> XY_Plane015
  Originals = -> [Pad028]
  Placement = pos=(0,0,0) rot=(1,0,0;1.5708rad)
FEATURE [Sketcher::SketchObject] Sketch074
  ExternalGeometry = -> [Mirrored]
  FullyConstrained = true
  MapMode = 5
  Placement = pos=(0,-2e-16,-0.833334) rot=(0,0,1;3.14159rad)
  Support = -> [Mirrored]
  sketch-geometry (5):
    g0: Circle CenterX=7.5 CenterY=50 CenterZ=0 NormalX=0 NormalY=0 NormalZ=1 AngleXU=0 Radius=1.69
    g1: Circle CenterX=7.5 CenterY=75 CenterZ=0 NormalX=0 NormalY=0 NormalZ=1 AngleXU=0 Radius=1.69
    g2: Circle CenterX=7.5 CenterY=100 CenterZ=0 NormalX=0 NormalY=0 NormalZ=1 AngleXU=0 Radius=1.69
    g3: LineSegment StartX=7.5 StartY=100 StartZ=0 EndX=7.5 EndY=75 EndZ=0
    g4: LineSegment StartX=7.5 StartY=75 StartZ=0 EndX=7.5 EndY=50 EndZ=0
  constraints (13):
    c: Equal(g2,g1)
    c: Equal(g2,g0)
    c: Diameter(g2) = 3.38
    c: Coincident(g3,g2)
    c: Coincident(g3,g1)
    c: Vertical(g3)
    c: Coincident(g4,g1)
    c: Coincident(g4,g0)
    c: Vertical(g4)
    c: DistanceY(g3,g3) = 25
    c: DistanceY(g-1,g0) = 50
    c: DistanceX(g0,g-3) = 7.5
    c: Equal(g3,g4)
FEATURE [PartDesign::Pad] Pad029  label="Pad-inside_holes"
  BaseFeature = -> Mirrored
  Direction = (0,-2e-16,1)
  Length = 10
  Length2 = 10
  Placement = pos=(0,0,0) rot=(1,0,0;1.5708rad)
  Profile = -> Sketch074
  ReferenceAxis = -> Sketch074 [N_Axis]
  Type = 0
FEATURE [PartDesign::Fillet] Fillet008
  Base = -> Pad029 [Edge5,Edge53,Edge47,Edge8]
  BaseFeature = -> Pad029
  Placement = pos=(0,0,0) rot=(1,0,0;1.5708rad)
  Radius = 1
  SupportTransform = false
  UseAllEdges = false
FEATURE [PartDesign::Fillet] Fillet009
  Base = -> Fillet008 [Edge43,Edge39,Edge62,Edge48]
  BaseFeature = -> Fillet008
  Placement = pos=(0,0,0) rot=(1,0,0;1.5708rad)
  Radius = 0.8
  SupportTransform = false
  UseAllEdges = false
FEATURE [PartDesign::Chamfer] Chamfer004
  Angle = 45
  Base = -> Fillet009 [Face25,Face24,Face23]
  BaseFeature = -> Fillet009
  ChamferType = 0
  FlipDirection = false
  Placement = pos=(0,0,0) rot=(1,0,0;1.5708rad)
  Size = 0.5
  Size2 = 1
  SupportTransform = false
  UseAllEdges = false
FEATURE [PartDesign::Chamfer] Chamfer005
  Angle = 45
  Base = -> Chamfer004 [Face53,Face54,Face55,Face52,Face50,Face46,Face45,Face47,Face51,Face49,Face48,Face44]
  BaseFeature = -> Chamfer004
  ChamferType = 0
  FlipDirection = false
  Placement = pos=(0,0,0) rot=(1,0,0;1.5708rad)
  Size = 0.5
  Size2 = 1
  SupportTransform = false
  UseAllEdges = false
FEATURE [PartDesign::Chamfer] Chamfer006
  Angle = 45
  Base = -> Chamfer005 [Face66,Face67,Face65,Face61,Face62,Face63,Face57,Face58,Face59,Face68,Face64,Face60]
  BaseFeature = -> Chamfer005
  ChamferType = 0
  FlipDirection = false
  Placement = pos=(0,0,0) rot=(1,0,0;1.5708rad)
  Size = 0.5
  Size2 = 1
  SupportTransform = false
  UseAllEdges = false
FEATURE [PartDesign::Body] Body016  label="Body-v3_slicer"
  Group = -> [Sketch072,Pad027,Sketch073,Pad028,Mirrored,Sketch074,Pad029,Fillet008,Fillet009,Chamfer004,Chamfer005,Chamfer006]
  Origin = -> Origin015
  Placement = pos=(-275,91,161.477) rot=(0,0,1;0rad)
  Tip = -> Chamfer006
